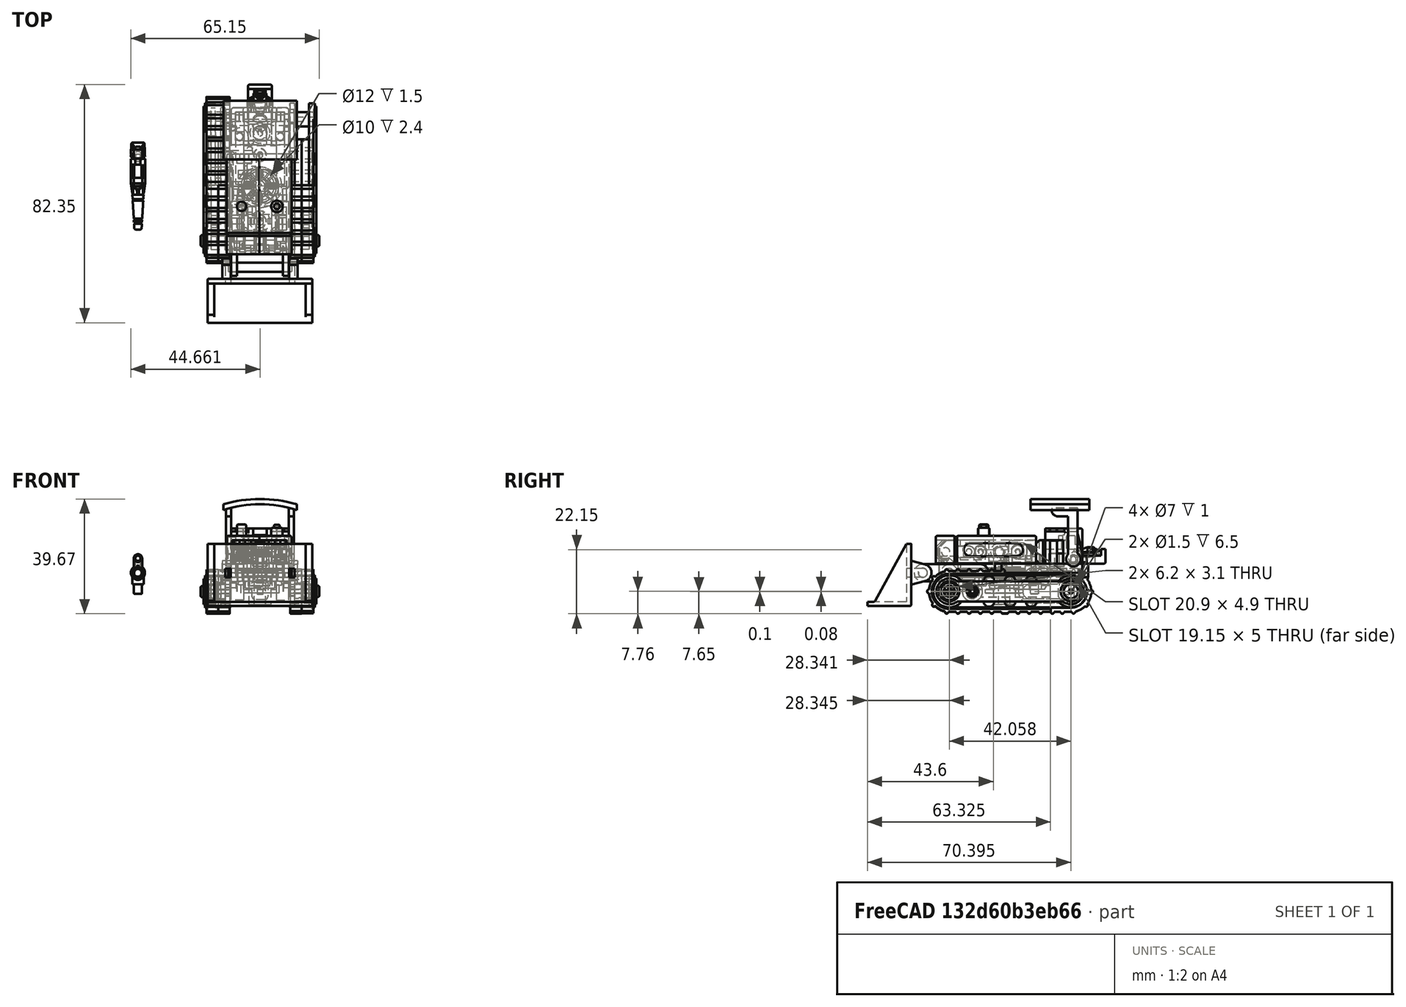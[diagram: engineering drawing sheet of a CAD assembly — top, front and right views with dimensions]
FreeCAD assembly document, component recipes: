
FREECAD ASSEMBLY — COMPONENT RECIPES ("Bonecrusher")

This assembly document has 22 components, labeled P0..P21 below (a component is one placed body or linked part). 22 of them carry a construction recipe — the FreeCAD feature program that regenerates the part from scratch, quoted from this document or its linked companion documents; the rest are supplied as boundary geometry only. No exploded tour is included for this assembly.
NOTE — this tour is split across 4 documents so each fits a 32k-token context. This is document 1: the component sections continue in the remaining 3 documents, each repeating the header above.
COMPONENT P0 — recipe-attached ("Right_Arm_Shield", modeled in this document).
Construction recipe (the document's own serialized feature program — sketch geometry with constraints, then the solid features built on it; lengths are millimeters unless a unit is written):

FEATURE [Sketcher::SketchObject] Sketch012
  ArcFitTolerance = 1e-06
  AttachmentSupport = -> [XY_Plane003]
  FullyConstrained = true
  MakeInternals = false
  MapMode = 5
  sketch-geometry (4):
    g0: LineSegment StartX=-34.7 StartY=4.75 StartZ=0 EndX=-34.7 EndY=-4.75 EndZ=0
    g1: LineSegment StartX=-34.7 StartY=-4.75 StartZ=0 EndX=0 EndY=-4.75 EndZ=0
    g2: LineSegment StartX=0 StartY=-4.75 StartZ=0 EndX=0 EndY=4.75 EndZ=0
    g3: LineSegment StartX=0 StartY=4.75 StartZ=0 EndX=-34.7 EndY=4.75 EndZ=0
  constraints (12):
    c: Coincident(g0,g1)
    c: Coincident(g1,g2)
    c: Coincident(g2,g3)
    c: Coincident(g3,g0)
    c: Vertical(g0)
    c: Vertical(g2)
    c: Horizontal(g1)
    c: Horizontal(g3)
    c: PointOnObject(g1,g-2)
    c: DistanceX(g3,g3) = 34.7
    c: DistanceY(g0,g0) = 9.5
    c: DistanceY(g-1,g2) = 4.75
FEATURE [PartDesign::Pad] Pad002
  Direction = (0,0,1)
  Length = 10.2
  Length2 = 10
  Profile = -> Sketch012
  ReferenceAxis = -> Sketch012 [N_Axis]
  Refine = true
  Suppressed = false
  Type = 0
FEATURE [Sketcher::SketchObject] Sketch013
  ArcFitTolerance = 1e-06
  AttachmentSupport = -> [Pad002]
  ExternalGeometry = -> [Pad002]
  FullyConstrained = true
  MakeInternals = false
  MapMode = 5
  Placement = pos=(0,0,10.2) rot=(0,0,1;0rad)
  sketch-geometry (4):
    g0: LineSegment StartX=-34.7 StartY=4.75 StartZ=0 EndX=-34.7 EndY=-3.25 EndZ=0
    g1: LineSegment StartX=-34.7 StartY=-3.25 StartZ=0 EndX=0 EndY=-3.25 EndZ=0
    g2: LineSegment StartX=0 StartY=-3.25 StartZ=0 EndX=0 EndY=4.75 EndZ=0
    g3: LineSegment StartX=0 StartY=4.75 StartZ=0 EndX=-34.7 EndY=4.75 EndZ=0
  constraints (11):
    c: Coincident(g0,g1)
    c: Coincident(g1,g2)
    c: Coincident(g2,g3)
    c: Coincident(g3,g0)
    c: Vertical(g0)
    c: Vertical(g2)
    c: Horizontal(g1)
    c: Horizontal(g3)
    c: Coincident(g0,g-3)
    c: PointOnObject(g1,g-4)
    c: DistanceY(g2,g2) = 8
FEATURE [PartDesign::Pocket] Pocket010
  BaseFeature = -> Pad002
  Direction = (0,0,-1)
  Length = 8.4
  Length2 = 5
  Profile = -> Sketch013
  ReferenceAxis = -> Sketch013 [N_Axis]
  Refine = true
  Suppressed = false
  Type = 0
FEATURE [Sketcher::SketchObject] Sketch014
  ArcFitTolerance = 1e-06
  AttachmentSupport = -> [Pocket010]
  ExternalGeometry = -> [Pocket010]
  FullyConstrained = true
  MakeInternals = false
  MapMode = 5
  Placement = pos=(0,0,1.8) rot=(0,0,1;0rad)
  sketch-geometry (4):
    g0: LineSegment StartX=-18.4 StartY=4.75 StartZ=0 EndX=-18.4 EndY=-3.25 EndZ=0
    g1: LineSegment StartX=-18.4 StartY=-3.25 StartZ=0 EndX=-7.1 EndY=-3.25 EndZ=0
    g2: LineSegment StartX=-7.1 StartY=-3.25 StartZ=0 EndX=-7.1 EndY=4.75 EndZ=0
    g3: LineSegment StartX=-7.1 StartY=4.75 StartZ=0 EndX=-18.4 EndY=4.75 EndZ=0
  constraints (12):
    c: Coincident(g0,g1)
    c: Coincident(g1,g2)
    c: Coincident(g2,g3)
    c: Coincident(g3,g0)
    c: Vertical(g0)
    c: Vertical(g2)
    c: Horizontal(g1)
    c: Horizontal(g3)
    c: DistanceX(g1,g-1) = 7.1
    c: DistanceX(g3,g3) = 11.3
    c: PointOnObject(g2,g-3)
    c: PointOnObject(g1,g-4)
FEATURE [PartDesign::Pad] Pad003
  BaseFeature = -> Pocket010
  Direction = (0,0,1)
  Length = 3.8
  Length2 = 10
  Profile = -> Sketch014
  ReferenceAxis = -> Sketch014 [N_Axis]
  Refine = true
  Suppressed = false
  Type = 0
FEATURE [Sketcher::SketchObject] Sketch015
  ArcFitTolerance = 1e-06
  AttachmentSupport = -> [Pad003]
  ExternalGeometry = -> [Pad003]
  FullyConstrained = true
  MakeInternals = false
  MapMode = 5
  Placement = pos=(0,0,1.8) rot=(0,0,1;0rad)
  sketch-geometry (1):
    g0: Circle CenterX=-22 CenterY=0.75 CenterZ=0 NormalX=0 NormalY=0 NormalZ=1 AngleXU=0 Radius=1.5
  constraints (3):
    c: Diameter(g0) = 3
    c: DistanceX(g-3,g0) = 12.7
    c: DistanceY(g0,g-3) = 4
FEATURE [PartDesign::Pad] Pad004
  BaseFeature = -> Pad003
  Direction = (0,0,1)
  Length = 7.5
  Length2 = 10
  Profile = -> Sketch015
  ReferenceAxis = -> Sketch015 [N_Axis]
  Refine = true
  Suppressed = false
  Type = 0
FEATURE [PartDesign::Fillet] Fillet002
  Base = -> Pad004 [Edge7,Edge2,Edge1,Edge10,Edge8]
  BaseFeature = -> Pad004
  Radius = 0.5
  Refine = true
  SupportTransform = false
  Suppressed = false
  UseAllEdges = false
FEATURE [Sketcher::SketchObject] Sketch016
  ArcFitTolerance = 1e-06
  AttachmentSupport = -> [Fillet002]
  ExternalGeometry = -> [Fillet002]
  FullyConstrained = true
  MakeInternals = false
  MapMode = 5
  Placement = pos=(0,0,5.6) rot=(0,0,1;0rad)
  sketch-geometry (4):
    g0: LineSegment StartX=-17.15 StartY=3.5 StartZ=0 EndX=-17.15 EndY=-3.25 EndZ=0
    g1: LineSegment StartX=-17.15 StartY=-3.25 StartZ=0 EndX=-8.35 EndY=-3.25 EndZ=0
    g2: LineSegment StartX=-8.35 StartY=-3.25 StartZ=0 EndX=-8.35 EndY=3.5 EndZ=0
    g3: LineSegment StartX=-8.35 StartY=3.5 StartZ=0 EndX=-17.15 EndY=3.5 EndZ=0
  constraints (12):
    c: Coincident(g0,g1)
    c: Coincident(g1,g2)
    c: Coincident(g2,g3)
    c: Coincident(g3,g0)
    c: Vertical(g0)
    c: Vertical(g2)
    c: Horizontal(g1)
    c: Horizontal(g3)
    c: DistanceY(g0,g-3) = 1.25
    c: PointOnObject(g0,g-4)
    c: DistanceX(g2,g-3) = 1.25
    c: DistanceX(g-3,g0) = 1.25
FEATURE [PartDesign::Pocket] Pocket011
  BaseFeature = -> Fillet002
  Direction = (0,0,-1)
  Length = 3.81
  Length2 = 5
  Profile = -> Sketch016
  ReferenceAxis = -> Sketch016 [N_Axis]
  Refine = true
  Suppressed = false
  Type = 0
FEATURE [Sketcher::SketchObject] Sketch017
  ArcFitTolerance = 1e-06
  AttachmentSupport = -> [Pocket011]
  ExternalGeometry = -> [Pocket011]
  FullyConstrained = false
  MakeInternals = false
  MapMode = 5
  Placement = pos=(0,0,1.79) rot=(0,0,1;0rad)
  sketch-geometry (4):
    g0: LineSegment StartX=-8.35 StartY=2.75 StartZ=0 EndX=-11.5 EndY=2.75 EndZ=0
    g1: ArcOfCircle CenterX=-11.5 CenterY=0.75 CenterZ=0 NormalX=0 NormalY=0 NormalZ=1 AngleXU=0 Radius=2 StartAngle=1.5708 EndAngle=4.71238
    g2: LineSegment StartX=-11.5 StartY=-1.25 StartZ=0 EndX=-8.35 EndY=-1.25 EndZ=0
    g3: LineSegment StartX=-8.35 StartY=-1.25 StartZ=0 EndX=-8.35 EndY=2.75 EndZ=0
  constraints (12):
    c: Horizontal(g0)
    c: Coincident(g1,g0)
    c: Coincident(g2,g1)
    c: Horizontal(g2)
    c: Coincident(g3,g2)
    c: Coincident(g3,g0)
    c: Vertical(g3)
    c: PointOnObject(g0,g-3)
    c: DistanceY(g2,g0) = 4
    c: DistanceY(g0,g-4) = 2
    c: Diameter(g1) = 4
    c: DistanceX(g0,g0) = 3.15
FEATURE [Sketcher::SketchObject] Sketch018
  ArcFitTolerance = 1e-06
  AttachmentSupport = -> [Pocket011]
  ExternalGeometry = -> [Pocket011]
  FullyConstrained = true
  MakeInternals = false
  MapMode = 5
  Placement = pos=(0,0,5.6) rot=(0,0,1;0rad)
  sketch-geometry (4):
    g0: LineSegment StartX=-8.35 StartY=2.75 StartZ=0 EndX=-8.35 EndY=-1.25 EndZ=0
    g1: LineSegment StartX=-8.35 StartY=-1.25 StartZ=0 EndX=-7.1 EndY=-1.25 EndZ=0
    g2: LineSegment StartX=-7.1 StartY=-1.25 StartZ=0 EndX=-7.1 EndY=2.75 EndZ=0
    g3: LineSegment StartX=-7.1 StartY=2.75 StartZ=0 EndX=-8.35 EndY=2.75 EndZ=0
  constraints (12):
    c: Coincident(g0,g1)
    c: Coincident(g1,g2)
    c: Coincident(g2,g3)
    c: Coincident(g3,g0)
    c: Vertical(g0)
    c: Vertical(g2)
    c: Horizontal(g1)
    c: Horizontal(g3)
    c: DistanceY(g2,g-3) = 2
    c: PointOnObject(g0,g-4)
    c: PointOnObject(g2,g-5)
    c: DistanceY(g1,g2) = 4
FEATURE [PartDesign::Pocket] Pocket012
  BaseFeature = -> Pocket011
  Direction = (0,0,-1)
  Length = 1.25
  Length2 = 5
  Profile = -> Sketch018
  ReferenceAxis = -> Sketch018 [N_Axis]
  Refine = true
  Suppressed = false
  Type = 0
FEATURE [PartDesign::Pad] Pad005
  BaseFeature = -> Pocket012
  Direction = (0,0,1)
  Length = 2.56
  Length2 = 10
  Profile = -> Sketch017
  ReferenceAxis = -> Sketch017 [N_Axis]
  Refine = true
  Suppressed = false
  Type = 0
FEATURE [Sketcher::SketchObject] Sketch019
  ArcFitTolerance = 1e-06
  AttachmentSupport = -> [Pad005]
  ExternalGeometry = -> [Pad005]
  FullyConstrained = true
  MakeInternals = false
  MapMode = 5
  Placement = pos=(0,0,1.79) rot=(0,0,1;0rad)
  sketch-geometry (1):
    g0: Circle CenterX=-15.5 CenterY=0.75 CenterZ=0 NormalX=0 NormalY=0 NormalZ=1 AngleXU=0 Radius=1.9
  constraints (3):
    c: DistanceY(g0,g-3) = 4
    c: Diameter(g0) = 3.8
    c: DistanceX(g-5,g0) = 1.65
FEATURE [PartDesign::Pad] Pad006
  BaseFeature = -> Pad005
  Direction = (0,0,1)
  Length = 5
  Length2 = 10
  Profile = -> Sketch019
  ReferenceAxis = -> Sketch019 [N_Axis]
  Refine = true
  Suppressed = false
  Type = 0
FEATURE [Sketcher::SketchObject] Sketch020
  ArcFitTolerance = 1e-06
  AttachmentSupport = -> [Pad006]
  ExternalGeometry = -> [Pad006]
  FullyConstrained = true
  MakeInternals = false
  MapMode = 5
  Placement = pos=(0,0,4.35) rot=(0,0,1;0rad)
  sketch-geometry (1):
    g0: Circle CenterX=-11.5 CenterY=0.75 CenterZ=0 NormalX=0 NormalY=0 NormalZ=1 AngleXU=0 Radius=1.05
  constraints (3):
    c: DistanceY(g0,g-4) = 2
    c: DistanceX(g0,g-3) = 4.4
    c: Diameter(g0) = 2.1
FEATURE [PartDesign::Pocket] Pocket014
  BaseFeature = -> Pad006
  Direction = (0,0,-1)
  Length = 2.56
  Length2 = 5
  Profile = -> Sketch020
  ReferenceAxis = -> Sketch020 [N_Axis]
  Refine = true
  Suppressed = false
  Type = 0
FEATURE [Sketcher::SketchObject] Sketch021
  ArcFitTolerance = 1e-06
  AttachmentSupport = -> [Pocket014]
  ExternalGeometry = -> [Pocket014]
  FullyConstrained = true
  MakeInternals = false
  MapMode = 5
  Placement = pos=(0,0,6.79) rot=(0,0,1;0rad)
  sketch-geometry (1):
    g0: Circle CenterX=-15.5 CenterY=0.75 CenterZ=0 NormalX=0 NormalY=0 NormalZ=1 AngleXU=0 Radius=0.75
  constraints (2):
    c: Diameter(g0) = 1.5
    c: Coincident(g0,g-3)
FEATURE [PartDesign::Pocket] Pocket015
  BaseFeature = -> Pocket014
  Direction = (0,0,-1)
  Length = 5
  Length2 = 5
  Profile = -> Sketch021
  ReferenceAxis = -> Sketch021 [N_Axis]
  Refine = true
  Suppressed = false
  Type = 0
FEATURE [Sketcher::SketchObject] Sketch022
  ArcFitTolerance = 1e-06
  AttachmentSupport = -> [Pocket015]
  ExternalGeometry = -> [Pocket015]
  FullyConstrained = true
  MakeInternals = false
  MapMode = 5
  Placement = pos=(0,0,0) rot=(1,0,0;3.14159rad)
  sketch-geometry (8):
    g0: ArcOfCircle CenterX=-27.95 CenterY=0 CenterZ=0 NormalX=0 NormalY=0 NormalZ=1 AngleXU=0 Radius=2.25 StartAngle=1.5708 EndAngle=4.71239
    g1: ArcOfCircle CenterX=-11.95 CenterY=1e-16 CenterZ=0 NormalX=0 NormalY=0 NormalZ=1 AngleXU=0 Radius=2.25 StartAngle=4.71239 EndAngle=7.85398
    g2: LineSegment StartX=-27.95 StartY=2.25 StartZ=0 EndX=-11.95 EndY=2.25 EndZ=0
    g3: LineSegment StartX=-27.95 StartY=-2.25 StartZ=0 EndX=-11.95 EndY=-2.25 EndZ=0
    g4: LineSegment StartX=-7.45 StartY=4.75 StartZ=0 EndX=-7.45 EndY=-4.75 EndZ=0
    g5: LineSegment StartX=-7.45 StartY=-4.75 StartZ=0 EndX=-6.45 EndY=-4.75 EndZ=0
    g6: LineSegment StartX=-6.45 StartY=-4.75 StartZ=0 EndX=-6.45 EndY=4.75 EndZ=0
    g7: LineSegment StartX=-6.45 StartY=4.75 StartZ=0 EndX=-7.45 EndY=4.75 EndZ=0
  constraints (22):
    c: Tangent(g0,g2) = 1.5708
    c: Tangent(g0,g3) = -1.5708
    c: Tangent(g1,g2) = 1.5708
    c: Tangent(g1,g3) = -1.5708
    c: Equal(g0,g1)
    c: Horizontal(g3)
    c: PointOnObject(g0,g-1)
    c: Diameter(g0) = 4.5
    c: DistanceX(g-3,g0) = 6.75
    c: DistanceX(g0,g1) = 16
    c: Coincident(g4,g5)
    c: Coincident(g5,g6)
    c: Coincident(g6,g7)
    c: Coincident(g7,g4)
    c: Vertical(g4)
    c: Vertical(g6)
    c: Horizontal(g5)
    c: Horizontal(g7)
    c: PointOnObject(g6,g-4)
    c: PointOnObject(g5,g-5)
    c: DistanceX(g1,g4) = 4.5
    c: DistanceX(g4,g6) = 1
FEATURE [PartDesign::Pocket] Pocket016
  BaseFeature = -> Pocket015
  Direction = (0,0,1)
  Length = 0.3
  Length2 = 5
  Profile = -> Sketch022
  ReferenceAxis = -> Sketch022 [N_Axis]
  Refine = true
  Suppressed = false
  Type = 0
FEATURE [Sketcher::SketchObject] Sketch023
  ArcFitTolerance = 1e-06
  AttachmentSupport = -> [Pocket016]
  ExternalGeometry = -> [Pocket016]
  FullyConstrained = true
  MakeInternals = false
  MapMode = 5
  Placement = pos=(0,-4.75,0) rot=(1,0,0;1.5708rad)
  sketch-geometry (4):
    g0: LineSegment StartX=-7.45 StartY=10.2 StartZ=0 EndX=-7.45 EndY=0 EndZ=0
    g1: LineSegment StartX=-7.45 StartY=0 StartZ=0 EndX=-6.45 EndY=0 EndZ=0
    g2: LineSegment StartX=-6.45 StartY=0 StartZ=0 EndX=-6.45 EndY=10.2 EndZ=0
    g3: LineSegment StartX=-6.45 StartY=10.2 StartZ=0 EndX=-7.45 EndY=10.2 EndZ=0
  constraints (11):
    c: Coincident(g0,g1)
    c: Coincident(g1,g2)
    c: Coincident(g2,g3)
    c: Coincident(g3,g0)
    c: Vertical(g0)
    c: Vertical(g2)
    c: Horizontal(g1)
    c: Horizontal(g3)
    c: DistanceX(g3,g3) = 1
    c: Coincident(g0,g-3)
    c: PointOnObject(g0,g-4)
FEATURE [PartDesign::Pocket] Pocket017
  BaseFeature = -> Pocket016
  Direction = (0,1,-2e-16)
  Length = 0.3
  Length2 = 5
  Profile = -> Sketch023
  ReferenceAxis = -> Sketch023 [N_Axis]
  Refine = true
  Suppressed = false
  Type = 0
FEATURE [PartDesign::Fillet] Fillet003
  Base = -> Pocket017 [Edge90,Edge91,Edge89,Edge92]
  BaseFeature = -> Pocket017
  Radius = 0.2
  Refine = true
  SupportTransform = false
  Suppressed = false
  UseAllEdges = false
FEATURE [PartDesign::Fillet] Fillet004
  Base = -> Fillet003 [Edge5,Edge94,Edge20,Edge19,Edge18,Edge17,Edge93,Edge97,Edge96,Edge95]
  BaseFeature = -> Fillet003
  Radius = 0.2
  Refine = true
  SupportTransform = false
  Suppressed = false
  UseAllEdges = false
FEATURE [Sketcher::SketchObject] Sketch036
  ArcFitTolerance = 1e-06
  AttachmentSupport = -> [Fillet004]
  ExternalGeometry = -> [Fillet004]
  FullyConstrained = true
  MakeInternals = false
  MapMode = 5
  Placement = pos=(0,-4.75,0) rot=(1,0,0;1.5708rad)
  sketch-geometry (1):
    g0: Circle CenterX=-16.6 CenterY=5.1 CenterZ=0 NormalX=0 NormalY=0 NormalZ=1 AngleXU=0 Radius=1.625
  constraints (3):
    c: Diameter(g0) = 3.25
    c: DistanceY(g0,g-3) = 5.1
    c: DistanceX(g0,g-4) = 16.6
FEATURE [PartDesign::Pad] Pad012
  BaseFeature = -> Fillet004
  Direction = (0,-1,2e-16)
  Length = 4
  Length2 = 10
  Profile = -> Sketch036
  ReferenceAxis = -> Sketch036 [N_Axis]
  Refine = true
  Suppressed = false
  Type = 0
FEATURE [PartDesign::Fillet] Fillet008
  Base = -> Pad012 [Edge116]
  BaseFeature = -> Pad012
  Radius = 0.5
  Refine = true
  SupportTransform = false
  Suppressed = false
  UseAllEdges = false
FEATURE [PartDesign::Fillet] Fillet020
  Base = -> Fillet008 [Edge89,Edge85]
  BaseFeature = -> Fillet008
  Radius = 0.5
  Refine = true
  SupportTransform = false
  Suppressed = false
  UseAllEdges = false
FEATURE [Sketcher::SketchObject] Sketch282
  ArcFitTolerance = 1e-06
  AttachmentSupport = -> [Fillet020]
  ExternalGeometry = -> [Fillet020]
  FullyConstrained = true
  MakeInternals = false
  MapMode = 5
  Placement = pos=(0,0,10.2) rot=(0,0,1;0rad)
  sketch-geometry (12):
    g0: LineSegment StartX=0 StartY=-3.25 StartZ=0 EndX=0 EndY=-4.25 EndZ=0
    g1: ArcOfCircle CenterX=-0.5 CenterY=-4.25 CenterZ=0 NormalX=0 NormalY=0 NormalZ=1 AngleXU=0 Radius=0.5 StartAngle=4.71239 EndAngle=6.28319
    g2: LineSegment StartX=-0.5 StartY=-4.75 StartZ=0 EndX=-6.25 EndY=-4.75 EndZ=0
    g3: ArcOfCircle CenterX=-6.25 CenterY=-4.55 CenterZ=0 NormalX=0 NormalY=0 NormalZ=1 AngleXU=0 Radius=0.2 StartAngle=3.14159 EndAngle=4.71239
    g4: LineSegment StartX=-6.45 StartY=-4.55 StartZ=0 EndX=-6.45 EndY=-4.45 EndZ=0
    g5: LineSegment StartX=-6.45 StartY=-4.45 StartZ=0 EndX=-7.45 EndY=-4.45 EndZ=0
    g6: LineSegment StartX=-7.45 StartY=-4.45 StartZ=0 EndX=-7.45 EndY=-4.55 EndZ=0
    g7: ArcOfCircle CenterX=-7.65 CenterY=-4.55 CenterZ=0 NormalX=0 NormalY=0 NormalZ=1 AngleXU=0 Radius=0.2 StartAngle=4.71239 EndAngle=6.28319
    g8: LineSegment StartX=-7.65 StartY=-4.75 StartZ=0 EndX=-34.2 EndY=-4.75 EndZ=0
    g9: ArcOfCircle CenterX=-34.2 CenterY=-4.25 CenterZ=0 NormalX=0 NormalY=0 NormalZ=1 AngleXU=0 Radius=0.5 StartAngle=3.14159 EndAngle=4.71239
    g10: LineSegment StartX=-34.7 StartY=-4.25 StartZ=0 EndX=-34.7 EndY=-3.25 EndZ=0
    g11: LineSegment StartX=-34.7 StartY=-3.25 StartZ=0 EndX=0 EndY=-3.25 EndZ=0
  constraints (24):
    c: Coincident(g0,g-14)
    c: Coincident(g0,g-14)
    c: Coincident(g1,g0)
    c: Tangent(g1,g-13) = -1.5708
    c: Coincident(g2,g1)
    c: Coincident(g2,g-12)
    c: Coincident(g3,g2)
    c: Tangent(g3,g-11) = -1.5708
    c: Coincident(g5,g4)
    c: Coincident(g5,g-9)
    c: Coincident(g6,g5)
    c: Coincident(g6,g-8)
    c: Coincident(g7,g6)
    c: Tangent(g7,g-7) = -1.5708
    c: Coincident(g9,g8)
    c: Tangent(g9,g-5) = -1.5708
    c: Coincident(g11,g10)
    c: Coincident(g11,g0)
    c: Coincident(g4,g3)
    c: Coincident(g8,g7)
    c: Coincident(g-6,g8)
    c: Coincident(g10,g-4)
    c: Coincident(g10,g9)
    c: Coincident(g4,g-10)
FEATURE [PartDesign::Pad] Pad161
  BaseFeature = -> Fillet020
  Direction = (0,0,1)
  Length = 1
  Length2 = 10
  Profile = -> Sketch282
  ReferenceAxis = -> Sketch282 [N_Axis]
  Refine = true
  Suppressed = false
  Type = 0
FEATURE [PartDesign::Body] Body002  label="Right_Arm_Shield"
  AllowCompound = false
  Group = -> [Sketch012,Pad002,Sketch013,Pocket010,Sketch014,Pad003,Sketch015,Pad004,Fillet002,Sketch016,Pocket011,Sketch017,Sketch018,Pocket012,Pad005,Sketch019,Pad006,Sketch020,Pocket014,Sketch021,Pocket015,Sketch022,Pocket016,Sketch023,Pocket017,Fillet003,Fillet004,Sketch036,Pad012,Fillet008,Fillet020,Sketch282,Pad161]
  Origin = -> Origin003
  Placement = pos=(26.75,-55.7,8) rot=(0.58,-0.58,0.58;4.18879rad)
  Tip = -> Pad161
COMPONENT P1 — recipe-attached ("Front_Torso", modeled in this document).
Construction recipe (the document's own serialized feature program — sketch geometry with constraints, then the solid features built on it; lengths are millimeters unless a unit is written):

FEATURE [Sketcher::SketchObject] Sketch080
  ArcFitTolerance = 1e-06
  AttachmentSupport = -> [XY_Plane010]
  FullyConstrained = true
  MakeInternals = false
  MapMode = 5
  sketch-geometry (20):
    g0: LineSegment StartX=10 StartY=7.75 StartZ=0 EndX=10 EndY=-18.25 EndZ=0
    g1: LineSegment StartX=7.75 StartY=-19.25 StartZ=0 EndX=7.75 EndY=-33.25 EndZ=0
    g2: LineSegment StartX=5.65 StartY=-34.25 StartZ=0 EndX=5.65 EndY=-39.75 EndZ=0
    g3: LineSegment StartX=-5.65 StartY=-39.75 StartZ=0 EndX=-5.65 EndY=-34.25 EndZ=0
    g4: LineSegment StartX=-7.75 StartY=-33.25 StartZ=0 EndX=-7.75 EndY=-19.25 EndZ=0
    g5: LineSegment StartX=-10 StartY=-18.25 StartZ=0 EndX=-10 EndY=7.75 EndZ=0
    g6: ArcOfCircle CenterX=-9 CenterY=-18.25 CenterZ=0 NormalX=0 NormalY=0 NormalZ=1 AngleXU=0 Radius=1 StartAngle=3.14159 EndAngle=4.71239
    g7: LineSegment StartX=-9 StartY=-19.25 StartZ=0 EndX=-7.75 EndY=-19.25 EndZ=0
    g8: ArcOfCircle CenterX=-6.75 CenterY=-33.25 CenterZ=0 NormalX=0 NormalY=0 NormalZ=1 AngleXU=0 Radius=1 StartAngle=3.14159 EndAngle=4.71239
    g9: LineSegment StartX=-6.75 StartY=-34.25 StartZ=0 EndX=-5.65 EndY=-34.25 EndZ=0
    g10: ArcOfCircle CenterX=6.75 CenterY=-33.25 CenterZ=0 NormalX=0 NormalY=0 NormalZ=1 AngleXU=0 Radius=1 StartAngle=4.71239 EndAngle=6.28319
    g11: LineSegment StartX=5.65 StartY=-34.25 StartZ=0 EndX=6.75 EndY=-34.25 EndZ=0
    g12: ArcOfCircle CenterX=-4.65 CenterY=-39.75 CenterZ=0 NormalX=0 NormalY=0 NormalZ=1 AngleXU=0 Radius=1 StartAngle=3.14159 EndAngle=4.71239
    g13: ArcOfCircle CenterX=4.65 CenterY=-39.75 CenterZ=0 NormalX=0 NormalY=0 NormalZ=1 AngleXU=0 Radius=1 StartAngle=4.71239 EndAngle=6.28319
    g14: LineSegment StartX=4.65 StartY=-40.75 StartZ=0 EndX=-4.65 EndY=-40.75 EndZ=0
    g15: ArcOfCircle CenterX=9 CenterY=-18.25 CenterZ=0 NormalX=0 NormalY=0 NormalZ=1 AngleXU=0 Radius=1 StartAngle=4.71239 EndAngle=6.28319
    g16: LineSegment StartX=9 StartY=-19.25 StartZ=0 EndX=7.75 EndY=-19.25 EndZ=0
    g17: ArcOfCircle CenterX=-9 CenterY=7.75 CenterZ=0 NormalX=0 NormalY=0 NormalZ=1 AngleXU=0 Radius=1 StartAngle=1.5708 EndAngle=3.14159
    g18: ArcOfCircle CenterX=9 CenterY=7.75 CenterZ=0 NormalX=0 NormalY=0 NormalZ=1 AngleXU=0 Radius=1 StartAngle=0 EndAngle=1.5708
    g19: LineSegment StartX=-9 StartY=8.75 StartZ=0 EndX=9 EndY=8.75 EndZ=0
  constraints (68):
    c: Vertical(g0)
    c: Vertical(g1)
    c: Vertical(g2)
    c: Vertical(g3)
    c: Vertical(g4)
    c: Vertical(g5)
    c: DistanceY(g0,g0) = 26
    c: DistanceY(g5,g5) = 26
    c: DistanceX(g1,g0) = 2.25
    c: DistanceX(g5,g4) = 2.25
    c: DistanceY(g1,g1) = 14
    c: DistanceY(g4,g4) = 14
    c: DistanceX(g4,g3) = 2.1
    c: DistanceX(g2,g1) = 2.1
    c: DistanceY(g3,g3) = 5.5
    c: DistanceY(g-1,g5) = 7.75
    c: DistanceX(g5,g0) = 20
    c: DistanceX(g5,g-1) = 10
    c: Coincident(g6,g5)
    c: Coincident(g7,g6)
    c: Coincident(g7,g4)
    c: Horizontal(g7)
    c: Diameter(g6) = 2
    c: DistanceX(g6,g6) = 0
    c: DistanceY(g6,g5) = 0
    c: Coincident(g8,g4)
    c: Coincident(g9,g8)
    c: Coincident(g9,g3)
    c: Horizontal(g9)
    c: Diameter(g8) = 2
    c: DistanceX(g8,g8) = 0
    c: DistanceY(g8,g4) = 0
    c: Coincident(g10,g1)
    c: Coincident(g11,g2)
    c: Coincident(g11,g10)
    c: Horizontal(g11)
    c: Diameter(g10) = 2
    c: DistanceX(g10,g10) = 0
    c: DistanceY(g10,g1) = 0
    c: Coincident(g12,g3)
    c: Coincident(g13,g2)
    c: Coincident(g14,g13)
    c: Coincident(g14,g12)
    c: Horizontal(g14)
    c: Diameter(g12) = 2
    c: Diameter(g13) = 2
    c: DistanceY(g12,g3) = 0
    c: DistanceY(g13,g2) = 0
    c: DistanceX(g13,g13) = 0
    c: DistanceX(g12,g12) = 0
    c: Coincident(g15,g0)
    c: Coincident(g16,g15)
    c: Coincident(g16,g1)
    c: Horizontal(g16)
    c: Diameter(g15) = 2
    c: DistanceY(g15,g0) = 0
    c: DistanceX(g15,g15) = 0
    c: DistanceY(g2,g2) = 5.5
    c: Coincident(g17,g5)
    c: Coincident(g18,g0)
    c: Coincident(g19,g17)
    c: Coincident(g19,g18)
    c: Horizontal(g19)
    c: Diameter(g18) = 2
    c: Diameter(g17) = 2
    c: DistanceX(g17,g17) = 0
    c: DistanceX(g18,g18) = 0
    c: DistanceY(g0,g18) = 0
FEATURE [PartDesign::Pad] Pad042
  Direction = (0,0,1)
  Length = 1.7
  Length2 = 10
  Profile = -> Sketch080
  ReferenceAxis = -> Sketch080 [N_Axis]
  Refine = true
  Suppressed = false
  Type = 0
FEATURE [PartDesign::Plane] DatumPlane012
  AttachmentSupport = -> [Pad042]
  Length = 61.4673
  MapMode = 5
  Placement = pos=(0,0,1.7) rot=(0,0,1;0rad)
  ResizeMode = 0
  Width = 77.2173
FEATURE [Sketcher::SketchObject] Sketch081
  ArcFitTolerance = 1e-06
  AttachmentSupport = -> [DatumPlane012]
  FullyConstrained = true
  MakeInternals = false
  MapMode = 5
  Placement = pos=(0,0,1.7) rot=(0,0,1;0rad)
  sketch-geometry (4):
    g0: LineSegment StartX=-4.5 StartY=8.75 StartZ=0 EndX=4.5 EndY=8.75 EndZ=0
    g1: LineSegment StartX=4.5 StartY=8.75 StartZ=0 EndX=4.5 EndY=10.75 EndZ=0
    g2: LineSegment StartX=4.5 StartY=10.75 StartZ=0 EndX=-4.5 EndY=10.75 EndZ=0
    g3: LineSegment StartX=-4.5 StartY=10.75 StartZ=0 EndX=-4.5 EndY=8.75 EndZ=0
  constraints (12):
    c: Coincident(g0,g1)
    c: Coincident(g1,g2)
    c: Coincident(g2,g3)
    c: Coincident(g3,g0)
    c: Horizontal(g0)
    c: Horizontal(g2)
    c: Vertical(g1)
    c: Vertical(g3)
    c: PointOnObject(g0,g-3)
    c: DistanceX(g2,g2) = 9
    c: DistanceY(g3,g3) = 2
    c: DistanceX(g0,g-3) = 5.5
FEATURE [PartDesign::Pad] Pad043
  BaseFeature = -> Pad042
  Direction = (0,0,1)
  Length = 4.8
  Length2 = 10
  Profile = -> Sketch081
  ReferenceAxis = -> Sketch081 [N_Axis]
  Refine = true
  Reversed = true
  Suppressed = false
  Type = 0
FEATURE [PartDesign::Plane] DatumPlane013
  AttachmentSupport = -> [Pad043]
  Length = 60
  MapMode = 5
  Placement = pos=(0,10.75,0) rot=(0,0.707107,0.707107;3.14159rad)
  ResizeMode = 0
  Width = 60
FEATURE [Sketcher::SketchObject] Sketch082
  ArcFitTolerance = 1e-06
  AttachmentSupport = -> [DatumPlane013]
  ExternalGeometry = -> [DatumPlane012,Pad043]
  FullyConstrained = true
  MakeInternals = false
  MapMode = 5
  Placement = pos=(0,10.75,0) rot=(0,0.707107,0.707107;3.14159rad)
  sketch-geometry (4):
    g0: LineSegment StartX=-3.1 StartY=1.7 StartZ=0 EndX=-3.1 EndY=-1.3 EndZ=0
    g1: LineSegment StartX=-3.1 StartY=-1.3 StartZ=0 EndX=3.1 EndY=-1.3 EndZ=0
    g2: LineSegment StartX=3.1 StartY=-1.3 StartZ=0 EndX=3.1 EndY=1.7 EndZ=0
    g3: LineSegment StartX=3.1 StartY=1.7 StartZ=0 EndX=-3.1 EndY=1.7 EndZ=0
  constraints (12):
    c: Coincident(g0,g1)
    c: Coincident(g1,g2)
    c: Coincident(g2,g3)
    c: Coincident(g3,g0)
    c: Vertical(g0)
    c: Vertical(g2)
    c: Horizontal(g1)
    c: Horizontal(g3)
    c: DistanceX(g-4,g0) = 1.4
    c: DistanceX(g2,g-5) = 1.4
    c: DistanceY(g-4,g0) = 1.8
    c: PointOnObject(g0,g-3)
FEATURE [PartDesign::Pocket] Pocket044
  BaseFeature = -> Pad043
  Direction = (0,-1,2e-16)
  Length = 2
  Length2 = 5
  Profile = -> Sketch082
  ReferenceAxis = -> Sketch082 [N_Axis]
  Refine = true
  Suppressed = false
  Type = 0
FEATURE [Sketcher::SketchObject] Sketch083
  ArcFitTolerance = 1e-06
  AttacherType = Attacher::AttachEngine3D
  AttachmentSupport = -> [DatumPlane012]
  FullyConstrained = true
  MakeInternals = false
  MapMode = 5
  Placement = pos=(0,0,1.7) rot=(0,0,1;0rad)
  sketch-geometry (4):
    g0: Circle CenterX=0 CenterY=0 CenterZ=0 NormalX=0 NormalY=0 NormalZ=1 AngleXU=0 Radius=0.75
    g1: Circle CenterX=-7.05 CenterY=-1.25 CenterZ=0 NormalX=0 NormalY=0 NormalZ=1 AngleXU=0 Radius=1.3
    g2: Circle CenterX=7.05 CenterY=-1.25 CenterZ=0 NormalX=0 NormalY=0 NormalZ=1 AngleXU=0 Radius=1.3
    g3: Circle CenterX=0 CenterY=-18.25 CenterZ=0 NormalX=0 NormalY=0 NormalZ=1 AngleXU=0 Radius=0.65
  constraints (11):
    c: Coincident(g0,g-1)
    c: Diameter(g0) = 1.5
    c: DistanceY(g1,g-3) = 10
    c: DistanceY(g2,g-4) = 10
    c: Diameter(g1) = 2.6
    c: Diameter(g2) = 2.6
    c: PointOnObject(g3,g-2)
    c: Diameter(g3) = 1.3
    c: DistanceY(g3,g-3) = 27
    c: DistanceX(g2,g-4) = 2.95
    c: DistanceX(g-3,g1) = 2.95
FEATURE [PartDesign::Pocket] Pocket045
  BaseFeature = -> Pocket044
  Direction = (0,0,-1)
  Length = 1.7
  Length2 = 5
  Profile = -> Sketch083
  ReferenceAxis = -> Sketch083 [N_Axis]
  Refine = true
  Suppressed = false
  Type = 0
FEATURE [Sketcher::SketchObject] Sketch084
  ArcFitTolerance = 1e-06
  AttachmentSupport = -> [DatumPlane012]
  FullyConstrained = true
  MakeInternals = false
  MapMode = 5
  Placement = pos=(0,0,1.7) rot=(0,0,1;0rad)
  sketch-geometry (1):
    g0: Circle CenterX=0 CenterY=0 CenterZ=0 NormalX=0 NormalY=0 NormalZ=1 AngleXU=0 Radius=2.5
  constraints (2):
    c: Coincident(g0,g-1)
    c: Diameter(g0) = 5
FEATURE [PartDesign::Pocket] Pocket046
  BaseFeature = -> Pocket045
  Direction = (0,0,-1)
  Length = 1
  Length2 = 5
  Profile = -> Sketch084
  ReferenceAxis = -> Sketch084 [N_Axis]
  Refine = true
  Suppressed = false
  Type = 0
FEATURE [Sketcher::SketchObject] Sketch085
  ArcFitTolerance = 1e-06
  AttachmentSupport = -> [DatumPlane012]
  ExternalGeometry = -> [Pocket046]
  FullyConstrained = true
  MakeInternals = false
  MapMode = 5
  Placement = pos=(0,0,1.7) rot=(0,0,1;0rad)
  sketch-geometry (4):
    g0: ArcOfCircle CenterX=-1.375 CenterY=4.95 CenterZ=0 NormalX=0 NormalY=0 NormalZ=1 AngleXU=0 Radius=1 StartAngle=1.5708 EndAngle=4.71239
    g1: ArcOfCircle CenterX=1.375 CenterY=4.95 CenterZ=0 NormalX=0 NormalY=0 NormalZ=1 AngleXU=0 Radius=1 StartAngle=4.71239 EndAngle=7.85398
    g2: LineSegment StartX=-1.375 StartY=5.95 StartZ=0 EndX=1.375 EndY=5.95 EndZ=0
    g3: LineSegment StartX=-1.375 StartY=3.95 StartZ=0 EndX=1.375 EndY=3.95 EndZ=0
  constraints (10):
    c: Tangent(g0,g2) = 1.5708
    c: Tangent(g0,g3) = -1.5708
    c: Tangent(g1,g2) = 1.5708
    c: Tangent(g1,g3) = -1.5708
    c: Equal(g0,g1)
    c: Horizontal(g3)
    c: DistanceY(g0,g-3) = 2.8
    c: Diameter(g0) = 2
    c: DistanceX(g0,g1) = 2.75
    c: DistanceX(g-1,g1) = 1.375
FEATURE [PartDesign::Pad] Pad044
  BaseFeature = -> Pocket046
  Direction = (0,0,1)
  Length = 0.5
  Length2 = 10
  Profile = -> Sketch085
  ReferenceAxis = -> Sketch085 [N_Axis]
  Refine = true
  Suppressed = false
  Type = 0
FEATURE [Sketcher::SketchObject] Sketch086
  ArcFitTolerance = 1e-06
  AttachmentSupport = -> [DatumPlane012]
  FullyConstrained = true
  MakeInternals = false
  MapMode = 5
  Placement = pos=(0,0,1.7) rot=(0,0,1;0rad)
  sketch-geometry (4):
    g0: LineSegment StartX=1.15 StartY=-40.75 StartZ=0 EndX=1.15 EndY=-27 EndZ=0
    g1: LineSegment StartX=1.15 StartY=-27 StartZ=0 EndX=-1.15 EndY=-27 EndZ=0
    g2: LineSegment StartX=-1.15 StartY=-27 StartZ=0 EndX=-1.15 EndY=-40.75 EndZ=0
    g3: LineSegment StartX=-1.15 StartY=-40.75 StartZ=0 EndX=1.15 EndY=-40.75 EndZ=0
  constraints (12):
    c: Coincident(g0,g1)
    c: Coincident(g1,g2)
    c: Coincident(g2,g3)
    c: Coincident(g3,g0)
    c: Vertical(g0)
    c: Vertical(g2)
    c: Horizontal(g1)
    c: Horizontal(g3)
    c: PointOnObject(g0,g-3)
    c: DistanceX(g1,g1) = 2.3
    c: DistanceY(g2,g2) = 13.75
    c: DistanceX(g-4,g2) = 4.5
FEATURE [PartDesign::Pad] Pad045
  BaseFeature = -> Pad044
  Direction = (0,0,1)
  Length = 2.5
  Length2 = 10
  Profile = -> Sketch086
  ReferenceAxis = -> Sketch086 [N_Axis]
  Refine = true
  Suppressed = false
  Type = 0
FEATURE [PartDesign::Plane] DatumPlane014
  AttachmentSupport = -> [Pad045]
  Length = 77.2173
  MapMode = 5
  Placement = pos=(1.15,0,0) rot=(0.57735,0.57735,0.57735;2.0944rad)
  ResizeMode = 0
  Width = 61.4673
FEATURE [Sketcher::SketchObject] Sketch087
  ArcFitTolerance = 1e-06
  AttachmentSupport = -> [DatumPlane014]
  ExternalGeometry = -> [Pad045]
  FullyConstrained = true
  MakeInternals = false
  MapMode = 5
  Placement = pos=(1.15,0,0) rot=(0.57735,0.57735,0.57735;2.0944rad)
  sketch-geometry (3):
    g0: LineSegment StartX=-27 StartY=1.7 StartZ=0 EndX=-27 EndY=4.2 EndZ=0
    g1: LineSegment StartX=-29.5 StartY=4.2 StartZ=0 EndX=-27 EndY=1.7 EndZ=0
    g2: LineSegment StartX=-27 StartY=4.2 StartZ=0 EndX=-29.5 EndY=4.2 EndZ=0
  constraints (7):
    c: Coincident(g0,g-4)
    c: Coincident(g0,g-4)
    c: PointOnObject(g1,g-3)
    c: Coincident(g1,g0)
    c: Angle(g-3,g1) = 2.35619
    c: Coincident(g2,g0)
    c: Coincident(g2,g1)
FEATURE [PartDesign::Pocket] Pocket047
  BaseFeature = -> Pad045
  Direction = (-1,0,0)
  Length = 2.3
  Length2 = 5
  Profile = -> Sketch087
  ReferenceAxis = -> Sketch087 [N_Axis]
  Refine = true
  Suppressed = false
  Type = 0
FEATURE [Sketcher::SketchObject] Sketch088
  ArcFitTolerance = 1e-06
  AttachmentSupport = -> [Pocket047]
  FullyConstrained = true
  MakeInternals = false
  MapMode = 5
  Placement = pos=(0,0,0) rot=(1,0,0;3.14159rad)
  sketch-geometry (6):
    g0: ArcOfCircle CenterX=-4.65 CenterY=39.75 CenterZ=0 NormalX=0 NormalY=0 NormalZ=1 AngleXU=0 Radius=1 StartAngle=1.5708 EndAngle=3.14159
    g1: ArcOfCircle CenterX=4.65 CenterY=39.75 CenterZ=0 NormalX=0 NormalY=0 NormalZ=1 AngleXU=0 Radius=1 StartAngle=-1.8e-15 EndAngle=1.5708
    g2: LineSegment StartX=-4.65 StartY=40.75 StartZ=0 EndX=4.65 EndY=40.75 EndZ=0
    g3: LineSegment StartX=5.65 StartY=34.25 StartZ=0 EndX=-5.65 EndY=34.25 EndZ=0
    g4: LineSegment StartX=5.65 StartY=39.75 StartZ=0 EndX=5.65 EndY=34.25 EndZ=0
    g5: LineSegment StartX=-5.65 StartY=39.75 StartZ=0 EndX=-5.65 EndY=34.25 EndZ=0
  constraints (16):
    c: Coincident(g0,g-3)
    c: Coincident(g0,g-4)
    c: Coincident(g2,g0)
    c: Coincident(g2,g1)
    c: Coincident(g4,g1)
    c: Vertical(g4)
    c: DistanceY(g4,g4) = 5.5
    c: Coincident(g5,g0)
    c: Vertical(g5)
    c: Coincident(g3,g5)
    c: Coincident(g3,g4)
    c: Coincident(g1,g-5)
    c: Coincident(g1,g-5)
    c: Horizontal(g3)
    c: Horizontal(g2)
    c: DistanceY(g0,g0) = 0
FEATURE [PartDesign::Pad] Pad046
  BaseFeature = -> Pocket047
  Direction = (0,0,-1)
  Length = 1.5
  Length2 = 10
  Profile = -> Sketch088
  ReferenceAxis = -> Sketch088 [N_Axis]
  Refine = true
  Suppressed = false
  Type = 0
FEATURE [Sketcher::SketchObject] Sketch089
  ArcFitTolerance = 1e-06
  AttachmentSupport = -> [Pad046]
  ExternalGeometry = -> [Pad046]
  FullyConstrained = true
  MakeInternals = false
  MapMode = 5
  Placement = pos=(0,0,0) rot=(1,0,0;3.14159rad)
  sketch-geometry (14):
    g0: LineSegment StartX=7.75 StartY=33.25 StartZ=0 EndX=7.75 EndY=19.25 EndZ=0
    g1: LineSegment StartX=7.75 StartY=19.25 StartZ=0 EndX=9 EndY=19.25 EndZ=0
    g2: ArcOfCircle CenterX=9 CenterY=18.25 CenterZ=0 NormalX=0 NormalY=0 NormalZ=1 AngleXU=0 Radius=1 StartAngle=0 EndAngle=1.5708
    g3: LineSegment StartX=10 StartY=18.25 StartZ=0 EndX=10 EndY=-7.75 EndZ=0
    g4: LineSegment StartX=9 StartY=-8.75 StartZ=0 EndX=-9 EndY=-8.75 EndZ=0
    g5: ArcOfCircle CenterX=-9 CenterY=-7.75 CenterZ=0 NormalX=0 NormalY=0 NormalZ=1 AngleXU=0 Radius=1 StartAngle=3.14159 EndAngle=4.71239
    g6: LineSegment StartX=-10 StartY=-7.75 StartZ=0 EndX=-10 EndY=18.25 EndZ=0
    g7: ArcOfCircle CenterX=-9 CenterY=18.25 CenterZ=0 NormalX=0 NormalY=0 NormalZ=1 AngleXU=0 Radius=1 StartAngle=1.5708 EndAngle=3.14159
    g8: LineSegment StartX=-9 StartY=19.25 StartZ=0 EndX=-7.75 EndY=19.25 EndZ=0
    g9: ArcOfCircle CenterX=-6.75 CenterY=33.25 CenterZ=0 NormalX=0 NormalY=0 NormalZ=1 AngleXU=0 Radius=1 StartAngle=1.5708 EndAngle=3.14159
    g10: ArcOfCircle CenterX=6.75 CenterY=33.25 CenterZ=0 NormalX=0 NormalY=0 NormalZ=1 AngleXU=0 Radius=1 StartAngle=9e-16 EndAngle=1.5708
    g11: LineSegment StartX=6.75 StartY=34.25 StartZ=0 EndX=-6.75 EndY=34.25 EndZ=0
    g12: LineSegment StartX=-7.75 StartY=33.25 StartZ=0 EndX=-7.75 EndY=19.25 EndZ=0
    g13: ArcOfCircle CenterX=9 CenterY=-7.75 CenterZ=0 NormalX=0 NormalY=0 NormalZ=1 AngleXU=0 Radius=1 StartAngle=4.71239 EndAngle=6.28319
  constraints (35):
    c: Coincident(g2,g-11)
    c: Coincident(g2,g1)
    c: Coincident(g2,g-11)
    c: Tangent(g3,g2) = 1.5708
    c: Coincident(g5,g-6)
    c: Coincident(g5,g4)
    c: Coincident(g5,g-6)
    c: Coincident(g6,g5)
    c: Coincident(g6,g-5)
    c: Coincident(g7,g-4)
    c: Coincident(g7,g6)
    c: Coincident(g8,g7)
    c: Coincident(g8,g-3)
    c: Horizontal(g8)
    c: Coincident(g0,g1)
    c: Radius(g9) = 1
    c: DistanceX(g9,g9) = 0
    c: DistanceY(g9,g9) = 0
    c: PointOnObject(g0,g-14)
    c: Coincident(g10,g0)
    c: Radius(g10) = 1
    c: DistanceY(g0,g10) = 0
    c: Tangent(g11,g10) = -1.5708
    c: Coincident(g11,g9)
    c: Coincident(g12,g9)
    c: Coincident(g12,g8)
    c: Vertical(g12)
    c: Coincident(g13,g3)
    c: Coincident(g13,g-9)
    c: Coincident(g4,g13)
    c: Horizontal(g4)
    c: Coincident(g4,g-9)
    c: Coincident(g0,g-14)
    c: Horizontal(g1)
    c: Coincident(g10,g-15)
FEATURE [PartDesign::Pad] Pad047
  BaseFeature = -> Pad046
  Direction = (0,0,-1)
  Length = 1.5
  Length2 = 10
  Profile = -> Sketch089
  ReferenceAxis = -> Sketch089 [N_Axis]
  Refine = true
  Suppressed = false
  Type = 0
FEATURE [Sketcher::SketchObject] Sketch090
  ArcFitTolerance = 1e-06
  AttachmentSupport = -> [Pad047]
  ExternalGeometry = -> [Pad047]
  FullyConstrained = true
  MakeInternals = false
  MapMode = 5
  Placement = pos=(0,0,-1.5) rot=(1,0,0;3.14159rad)
  sketch-geometry (22):
    g0: ArcOfCircle CenterX=-4.1 CenterY=-8.25 CenterZ=0 NormalX=0 NormalY=0 NormalZ=1 AngleXU=0 Radius=1 StartAngle=0 EndAngle=1.5708
    g1: LineSegment StartX=-3.1 StartY=-8.25 StartZ=0 EndX=-3.1 EndY=-8.75 EndZ=0
    g2: ArcOfCircle CenterX=-7.25 CenterY=18.75 CenterZ=0 NormalX=0 NormalY=0 NormalZ=1 AngleXU=0 Radius=1 StartAngle=4.71239 EndAngle=6.28319
    g3: LineSegment StartX=-6.25 StartY=18.75 StartZ=0 EndX=-6.25 EndY=32.75 EndZ=0
    g4: LineSegment StartX=-3.1 StartY=-8.75 StartZ=0 EndX=3.1 EndY=-8.75 EndZ=0
    g5: LineSegment StartX=3.1 StartY=-8.75 StartZ=0 EndX=3.1 EndY=-8.25 EndZ=0
    g6: ArcOfCircle CenterX=4.1 CenterY=-8.25 CenterZ=0 NormalX=0 NormalY=0 NormalZ=1 AngleXU=0 Radius=1 StartAngle=1.5708 EndAngle=3.14159
    g7: LineSegment StartX=4.1 StartY=-7.25 StartZ=0 EndX=8.5 EndY=-7.25 EndZ=0
    g8: LineSegment StartX=8.5 StartY=-7.25 StartZ=0 EndX=8.5 EndY=17.75 EndZ=0
    g9: LineSegment StartX=8.5 StartY=17.75 StartZ=0 EndX=7.25 EndY=17.75 EndZ=0
    g10: ArcOfCircle CenterX=7.25 CenterY=18.75 CenterZ=0 NormalX=0 NormalY=0 NormalZ=1 AngleXU=0 Radius=1 StartAngle=3.14159 EndAngle=4.71239
    g11: LineSegment StartX=6.25 StartY=18.75 StartZ=0 EndX=6.25 EndY=32.75 EndZ=0
    g12: LineSegment StartX=-6.25 StartY=32.75 StartZ=0 EndX=-5.15 EndY=32.75 EndZ=0
    g13: ArcOfCircle CenterX=-5.15 CenterY=33.75 CenterZ=0 NormalX=0 NormalY=0 NormalZ=1 AngleXU=0 Radius=1 StartAngle=4.71239 EndAngle=6.28319
    g14: LineSegment StartX=-4.15 StartY=33.75 StartZ=0 EndX=-4.15 EndY=34.25 EndZ=0
    g15: LineSegment StartX=-4.15 StartY=34.25 StartZ=0 EndX=4.15 EndY=34.25 EndZ=0
    g16: LineSegment StartX=4.15 StartY=34.25 StartZ=0 EndX=4.15 EndY=33.75 EndZ=0
    g17: ArcOfCircle CenterX=5.15 CenterY=33.75 CenterZ=0 NormalX=0 NormalY=0 NormalZ=1 AngleXU=0 Radius=1 StartAngle=3.14159 EndAngle=4.71239
    g18: LineSegment StartX=5.15 StartY=32.75 StartZ=0 EndX=6.25 EndY=32.75 EndZ=0
    g19: LineSegment StartX=-4.1 StartY=-7.25 StartZ=0 EndX=-8.5 EndY=-7.25 EndZ=0
    g20: LineSegment StartX=-8.5 StartY=-7.25 StartZ=0 EndX=-8.5 EndY=17.75 EndZ=0
    g21: LineSegment StartX=-7.25 StartY=17.75 StartZ=0 EndX=-8.5 EndY=17.75 EndZ=0
  constraints (72):
    c: Coincident(g1,g0)
    c: Diameter(g0) = 2
    c: DistanceX(g0,g0) = 0
    c: DistanceY(g0,g0) = 0
    c: Vertical(g1)
    c: Coincident(g3,g2)
    c: Vertical(g3)
    c: DistanceX(g-10,g2) = 1.5
    c: DistanceX(g2,g2) = 0
    c: DistanceY(g2,g2) = 0
    c: Diameter(g2) = 2
    c: Coincident(g4,g1)
    c: Horizontal(g4)
    c: DistanceX(g4,g-6) = 1.4
    c: DistanceX(g-8,g1) = 1.4
    c: Coincident(g5,g4)
    c: Vertical(g5)
    c: Coincident(g6,g5)
    c: Coincident(g7,g6)
    c: Horizontal(g7)
    c: Coincident(g8,g7)
    c: Vertical(g8)
    c: Coincident(g9,g8)
    c: Horizontal(g9)
    c: Coincident(g10,g9)
    c: Coincident(g11,g10)
    c: Vertical(g11)
    c: Coincident(g12,g3)
    c: Horizontal(g12)
    c: Coincident(g13,g12)
    c: Coincident(g14,g13)
    c: Vertical(g14)
    c: Coincident(g15,g14)
    c: Horizontal(g15)
    c: Coincident(g16,g15)
    c: Coincident(g17,g16)
    c: Coincident(g18,g17)
    c: Coincident(g18,g11)
    c: DistanceX(g15,g-18) = 1.5
    c: Radius(g17) = 1
    c: Horizontal(g18)
    c: Vertical(g16)
    c: DistanceX(g11,g-13) = 1.5
    c: DistanceY(g17,g-18) = 1.5
    c: Radius(g10) = 1
    c: DistanceY(g8,g-15) = 1.5
    c: DistanceX(g8,g-15) = 1.5
    c: DistanceX(g10,g9) = 0
    c: DistanceY(g10,g10) = 0
    c: Radius(g6) = 1
    c: DistanceY(g-16,g7) = 1.5
    c: DistanceX(g6,g6) = 0
    c: DistanceY(g5,g6) = 0
    c: DistanceY(g4,g-6) = 0
    c: Radius(g13) = 1
    c: DistanceX(g12,g13) = 0
    c: DistanceY(g13,g13) = 0
    c: DistanceY(g3,g-11) = 1.5
    c: DistanceX(g-17,g14) = 1.5
    c: DistanceY(g14,g-17) = 0
    c: DistanceY(g16,g17) = 0
    c: DistanceX(g17,g17) = 0
    c: Coincident(g19,g0)
    c: Horizontal(g19)
    c: Coincident(g20,g19)
    c: Vertical(g20)
    c: Coincident(g21,g2)
    c: Coincident(g21,g20)
    c: Horizontal(g21)
    c: DistanceX(g-9,g20) = 1.5
    c: DistanceY(g-8,g19) = 1.5
    c: DistanceY(g20,g-10) = 1.5
FEATURE [PartDesign::Pocket] Pocket048
  BaseFeature = -> Pad047
  Direction = (0,0,1)
  Length = 1.5
  Length2 = 5
  Profile = -> Sketch090
  ReferenceAxis = -> Sketch090 [N_Axis]
  Refine = true
  Suppressed = false
  Type = 0
FEATURE [Sketcher::SketchObject] Sketch092
  ArcFitTolerance = 1e-06
  AttachmentSupport = -> [Pocket048]
  FullyConstrained = true
  MakeInternals = false
  MapMode = 5
  Placement = pos=(0,0,-4e-16) rot=(1,0,0;3.14159rad)
  sketch-geometry (1):
    g0: Circle CenterX=0 CenterY=0 CenterZ=0 NormalX=0 NormalY=0 NormalZ=1 AngleXU=0 Radius=3.475
  constraints (2):
    c: Coincident(g0,g-1)
    c: Diameter(g0) = 6.95
FEATURE [PartDesign::Pad] Pad048
  BaseFeature = -> Pocket048
  Direction = (0,0,-1)
  Length = 1.5
  Length2 = 10
  Profile = -> Sketch092
  ReferenceAxis = -> Sketch092 [N_Axis]
  Refine = true
  Suppressed = false
  Type = 0
FEATURE [Sketcher::SketchObject] Sketch093
  ArcFitTolerance = 1e-06
  AttachmentSupport = -> [Pad048]
  FullyConstrained = true
  MakeInternals = false
  MapMode = 5
  Placement = pos=(0,0,-1.5) rot=(1,0,0;3.14159rad)
  sketch-geometry (1):
    g0: Circle CenterX=0 CenterY=0 CenterZ=0 NormalX=0 NormalY=0 NormalZ=1 AngleXU=0 Radius=2.2
  constraints (2):
    c: Coincident(g0,g-1)
    c: Diameter(g0) = 4.4
FEATURE [PartDesign::Pocket] Pocket050
  BaseFeature = -> Pad048
  Direction = (0,0,1)
  Length = 1.5
  Length2 = 5
  Profile = -> Sketch093
  ReferenceAxis = -> Sketch093 [N_Axis]
  Refine = true
  Suppressed = false
  Type = 0
FEATURE [Sketcher::SketchObject] Sketch094
  ArcFitTolerance = 1e-06
  AttachmentSupport = -> [Pocket050]
  ExternalGeometry = -> [Pocket050]
  FullyConstrained = true
  MakeInternals = false
  MapMode = 5
  Placement = pos=(0,0,-4e-16) rot=(1,0,0;3.14159rad)
  sketch-geometry (2):
    g0: Circle CenterX=0 CenterY=18.25 CenterZ=0 NormalX=0 NormalY=0 NormalZ=1 AngleXU=0 Radius=1.7
    g1: Circle CenterX=0 CenterY=30.55 CenterZ=0 NormalX=0 NormalY=0 NormalZ=1 AngleXU=0 Radius=2.2
  constraints (5):
    c: Diameter(g0) = 3.4
    c: PointOnObject(g1,g-2)
    c: Diameter(g1) = 4.4
    c: DistanceY(g1,g-3) = 10.2
    c: Coincident(g0,g-4)
FEATURE [PartDesign::Pad] Pad049
  BaseFeature = -> Pocket050
  Direction = (0,0,-1)
  Length = 4
  Length2 = 10
  Profile = -> Sketch094
  ReferenceAxis = -> Sketch094 [N_Axis]
  Refine = true
  Suppressed = false
  Type = 0
FEATURE [Sketcher::SketchObject] Sketch095
  ArcFitTolerance = 1e-06
  AttachmentSupport = -> [Pad049]
  ExternalGeometry = -> [Pad049]
  FullyConstrained = true
  MakeInternals = false
  MapMode = 5
  Placement = pos=(0,0,-4) rot=(1,0,0;3.14159rad)
  sketch-geometry (1):
    g0: Circle CenterX=0 CenterY=30.55 CenterZ=0 NormalX=0 NormalY=0 NormalZ=1 AngleXU=0 Radius=0.75
  constraints (2):
    c: Coincident(g0,g-3)
    c: Diameter(g0) = 1.5
FEATURE [PartDesign::Pocket] Pocket051
  BaseFeature = -> Pad049
  Direction = (0,0,1)
  Length = 4
  Length2 = 5
  Profile = -> Sketch095
  ReferenceAxis = -> Sketch095 [N_Axis]
  Refine = true
  Suppressed = false
  Type = 0
FEATURE [Sketcher::SketchObject] Sketch096
  ArcFitTolerance = 1e-06
  AttachmentSupport = -> [Pocket051]
  ExternalGeometry = -> [Pocket051]
  FullyConstrained = true
  MakeInternals = false
  MapMode = 5
  Placement = pos=(0,0,-4e-16) rot=(1,0,0;3.14159rad)
  sketch-geometry (16):
    g0: ArcOfCircle CenterX=-3 CenterY=18.25 CenterZ=0 NormalX=0 NormalY=0 NormalZ=1 AngleXU=0 Radius=0.7 StartAngle=4.71239 EndAngle=7.85398
    g1: ArcOfCircle CenterX=-5 CenterY=18.25 CenterZ=0 NormalX=0 NormalY=0 NormalZ=1 AngleXU=0 Radius=0.7 StartAngle=1.5708 EndAngle=4.71239
    g2: LineSegment StartX=-3 StartY=17.55 StartZ=0 EndX=-5 EndY=17.55 EndZ=0
    g3: LineSegment StartX=-3 StartY=18.95 StartZ=0 EndX=-5 EndY=18.95 EndZ=0
    g4: ArcOfCircle CenterX=3 CenterY=18.25 CenterZ=0 NormalX=0 NormalY=0 NormalZ=1 AngleXU=0 Radius=0.7 StartAngle=1.5708 EndAngle=4.71239
    g5: ArcOfCircle CenterX=5 CenterY=18.25 CenterZ=0 NormalX=0 NormalY=0 NormalZ=1 AngleXU=0 Radius=0.7 StartAngle=4.71239 EndAngle=7.85398
    g6: LineSegment StartX=3 StartY=18.95 StartZ=0 EndX=5 EndY=18.95 EndZ=0
    g7: LineSegment StartX=3 StartY=17.55 StartZ=0 EndX=5 EndY=17.55 EndZ=0
    g8: ArcOfCircle CenterX=0 CenterY=21.25 CenterZ=0 NormalX=0 NormalY=0 NormalZ=1 AngleXU=0 Radius=0.7 StartAngle=3.14159 EndAngle=6.28319
    g9: ArcOfCircle CenterX=0 CenterY=23.25 CenterZ=0 NormalX=0 NormalY=0 NormalZ=1 AngleXU=0 Radius=0.7 StartAngle=5e-16 EndAngle=3.14159
    g10: LineSegment StartX=-0.7 StartY=21.25 StartZ=0 EndX=-0.7 EndY=23.25 EndZ=0
    g11: LineSegment StartX=0.7 StartY=21.25 StartZ=0 EndX=0.7 EndY=23.25 EndZ=0
    g12: ArcOfCircle CenterX=0 CenterY=15.25 CenterZ=0 NormalX=0 NormalY=0 NormalZ=1 AngleXU=0 Radius=0.7 StartAngle=-9e-16 EndAngle=3.14159
    g13: ArcOfCircle CenterX=0 CenterY=13.25 CenterZ=0 NormalX=0 NormalY=0 NormalZ=1 AngleXU=0 Radius=0.7 StartAngle=3.14159 EndAngle=6.28319
    g14: LineSegment StartX=0.7 StartY=15.25 StartZ=0 EndX=0.7 EndY=13.25 EndZ=0
    g15: LineSegment StartX=-0.7 StartY=15.25 StartZ=0 EndX=-0.7 EndY=13.25 EndZ=0
  constraints (40):
    c: Tangent(g0,g2) = 1.5708
    c: Tangent(g0,g3) = -1.5708
    c: Tangent(g1,g2) = 1.5708
    c: Tangent(g1,g3) = -1.5708
    c: Equal(g0,g1)
    c: Horizontal(g3)
    c: Tangent(g4,g6) = 1.5708
    c: Tangent(g4,g7) = -1.5708
    c: Tangent(g5,g6) = 1.5708
    c: Tangent(g5,g7) = -1.5708
    c: Equal(g4,g5)
    c: Horizontal(g7)
    c: Tangent(g8,g10) = 1.5708
    c: Tangent(g8,g11) = -1.5708
    c: Tangent(g9,g10) = 1.5708
    c: Tangent(g9,g11) = -1.5708
    c: Equal(g8,g9)
    c: Vertical(g11)
    c: PointOnObject(g8,g-2)
    c: Tangent(g12,g14) = 1.5708
    c: Tangent(g12,g15) = -1.5708
    c: Tangent(g13,g14) = 1.5708
    c: Tangent(g13,g15) = -1.5708
    c: Equal(g12,g13)
    c: Vertical(g15)
    c: Diameter(g1) = 1.4
    c: Diameter(g8) = 1.4
    c: Diameter(g4) = 1.4
    c: Diameter(g12) = 1.4
    c: Distance(g12,g13) = 2
    c: Distance(g0,g1) = 2
    c: Distance(g8,g9) = 2
    c: Distance(g4,g5) = 2
    c: DistanceX(g0,g-3) = 3
    c: DistanceX(g-3,g4) = 3
    c: DistanceY(g12,g-3) = 3
    c: DistanceY(g-3,g8) = 3
    c: PointOnObject(g12,g-2)
    c: DistanceY(g0,g-3) = 0
    c: DistanceY(g4,g-3) = 0
FEATURE [PartDesign::Pad] Pad050
  BaseFeature = -> Pocket051
  Direction = (0,0,-1)
  Length = 0.4
  Length2 = 10
  Profile = -> Sketch096
  ReferenceAxis = -> Sketch096 [N_Axis]
  Refine = true
  Suppressed = false
  Type = 0
FEATURE [Sketcher::SketchObject] Sketch097
  ArcFitTolerance = 1e-06
  AttachmentSupport = -> [Pad050]
  FullyConstrained = true
  MakeInternals = false
  MapMode = 5
  Placement = pos=(5.65,0,-4.7e-15) rot=(0.57735,0.57735,0.57735;2.0944rad)
  sketch-geometry (1):
    g0: Circle CenterX=-37.25 CenterY=-1.5 CenterZ=0 NormalX=0 NormalY=0 NormalZ=1 AngleXU=0 Radius=1.5
  constraints (3):
    c: Diameter(g0) = 3
    c: PointOnObject(g0,g-3)
    c: DistanceX(g0,g-3) = 2.5
FEATURE [PartDesign::Pocket] Pocket052
  BaseFeature = -> Pad050
  Direction = (-1,0,0)
  Length = 12
  Length2 = 5
  Profile = -> Sketch097
  ReferenceAxis = -> Sketch097 [N_Axis]
  Refine = true
  Suppressed = false
  Type = 0
FEATURE [Sketcher::SketchObject] Sketch098
  ArcFitTolerance = 1e-06
  AttachmentSupport = -> [Pocket052]
  ExternalGeometry = -> [Pocket052]
  FullyConstrained = true
  MakeInternals = false
  MapMode = 5
  Placement = pos=(7.75,0,0) rot=(0.57735,0.57735,0.57735;2.0944rad)
  sketch-geometry (1):
    g0: Circle CenterX=-26.65 CenterY=-1.5 CenterZ=0 NormalX=0 NormalY=0 NormalZ=1 AngleXU=0 Radius=1.5
  constraints (3):
    c: Tangent(g0,g-1)
    c: DistanceX(g-3,g0) = 6.6
    c: PointOnObject(g0,g-3)
FEATURE [PartDesign::Pocket] Pocket053
  BaseFeature = -> Pocket052
  Direction = (-1,0,0)
  Length = 16
  Length2 = 5
  Profile = -> Sketch098
  ReferenceAxis = -> Sketch098 [N_Axis]
  Refine = true
  Suppressed = false
  Type = 0
FEATURE [Sketcher::SketchObject] Sketch099
  ArcFitTolerance = 1e-06
  AttachmentSupport = -> [Pocket053]
  FullyConstrained = true
  MakeInternals = false
  MapMode = 5
  Placement = pos=(7.75,0,0) rot=(0.57735,0.57735,0.57735;2.0944rad)
  sketch-geometry (4):
    g0: LineSegment StartX=-24.75 StartY=1.7 StartZ=0 EndX=-24.75 EndY=-1.5 EndZ=0
    g1: LineSegment StartX=-24.75 StartY=-1.5 StartZ=0 EndX=-21.5 EndY=-1.5 EndZ=0
    g2: LineSegment StartX=-21.5 StartY=-1.5 StartZ=0 EndX=-21.5 EndY=1.7 EndZ=0
    g3: LineSegment StartX=-21.5 StartY=1.7 StartZ=0 EndX=-24.75 EndY=1.7 EndZ=0
  constraints (12):
    c: Coincident(g0,g1)
    c: Coincident(g1,g2)
    c: Coincident(g2,g3)
    c: Coincident(g3,g0)
    c: Vertical(g0)
    c: Vertical(g2)
    c: Horizontal(g1)
    c: Horizontal(g3)
    c: PointOnObject(g0,g-3)
    c: PointOnObject(g1,g-4)
    c: DistanceX(g0,g2) = 3.25
    c: DistanceX(g2,g-3) = 2.25
FEATURE [PartDesign::Pad] Pad051
  BaseFeature = -> Pocket053
  Direction = (1,0,0)
  Length = 0.2
  Length2 = 10
  Profile = -> Sketch099
  ReferenceAxis = -> Sketch099 [N_Axis]
  Refine = true
  Suppressed = false
  Type = 0
FEATURE [PartDesign::Body] Body009  label="Front_Torso"
  AllowCompound = false
  Group = -> [Sketch080,Pad042,DatumPlane012,Sketch081,Pad043,DatumPlane013,Sketch082,Pocket044,Sketch083,Pocket045,Sketch084,Pocket046,Sketch085,Pad044,Sketch086,Pad045,DatumPlane014,Sketch087,Pocket047,Sketch088,Pad046,Sketch089,Pad047,Sketch090,Pocket048,Sketch092,Pad048,Sketch093,Pocket050,Sketch094,Pad049,Sketch095,Pocket051,Sketch096,Pad050,Sketch097,Pocket052,Sketch098,Pocket053,Sketch099,Pad051,+24 more]
  Origin = -> Origin010
  Placement = pos=(38.2,-13.75,1.5) rot=(0,0,1;0rad)
  Tip = -> Pocket169
COMPONENT P2 — recipe-attached ("Chest", modeled in this document).
Construction recipe (the document's own serialized feature program — sketch geometry with constraints, then the solid features built on it; lengths are millimeters unless a unit is written):

FEATURE [Sketcher::SketchObject] Sketch102
  ArcFitTolerance = 1e-06
  AttachmentSupport = -> [YZ_Plane012]
  FullyConstrained = true
  MakeInternals = false
  MapMode = 5
  Placement = pos=(0,0,0) rot=(0.57735,0.57735,0.57735;2.0944rad)
  sketch-geometry (4):
    g0: LineSegment StartX=12.8 StartY=0 StartZ=0 EndX=12.8 EndY=12.1 EndZ=0
    g1: LineSegment StartX=12.8 StartY=12.1 StartZ=0 EndX=0 EndY=12.1 EndZ=0
    g2: LineSegment StartX=0 StartY=12.1 StartZ=0 EndX=0 EndY=0 EndZ=0
    g3: LineSegment StartX=0 StartY=0 StartZ=0 EndX=12.8 EndY=0 EndZ=0
  constraints (12):
    c: Coincident(g0,g1)
    c: Coincident(g1,g2)
    c: Coincident(g2,g3)
    c: Coincident(g3,g0)
    c: Vertical(g0)
    c: Vertical(g2)
    c: Horizontal(g1)
    c: Horizontal(g3)
    c: PointOnObject(g0,g-1)
    c: PointOnObject(g1,g-2)
    c: DistanceX(g1,g0) = 12.8
    c: DistanceY(g2,g1) = 12.1
FEATURE [PartDesign::Pad] Pad053
  Direction = (1,0,0)
  Length = 20
  Length2 = 10
  Placement = pos=(0,0,0) rot=(1,1,1;2.0944rad)
  Profile = -> Sketch102
  ReferenceAxis = -> Sketch102 [N_Axis]
  Refine = true
  Suppressed = false
  Type = 0
FEATURE [Sketcher::SketchObject] Sketch104
  ArcFitTolerance = 1e-06
  AttachmentSupport = -> [Pad053]
  ExternalGeometry = -> [Pad053]
  FullyConstrained = true
  MakeInternals = false
  MapMode = 5
  Placement = pos=(0,2.7e-15,12.1) rot=(0,0,-1;1.5708rad)
  sketch-geometry (4):
    g0: LineSegment StartX=0 StartY=14.05 StartZ=0 EndX=-4.75 EndY=14.05 EndZ=0
    g1: LineSegment StartX=-4.75 StartY=14.05 StartZ=0 EndX=-4.75 EndY=5.95 EndZ=0
    g2: LineSegment StartX=-4.75 StartY=5.95 StartZ=0 EndX=0 EndY=5.95 EndZ=0
    g3: LineSegment StartX=0 StartY=5.95 StartZ=0 EndX=0 EndY=14.05 EndZ=0
  constraints (12):
    c: Coincident(g0,g1)
    c: Coincident(g1,g2)
    c: Coincident(g2,g3)
    c: Coincident(g3,g0)
    c: Horizontal(g0)
    c: Horizontal(g2)
    c: Vertical(g1)
    c: Vertical(g3)
    c: PointOnObject(g0,g-2)
    c: DistanceX(g0,g0) = 4.75
    c: DistanceY(g1,g1) = 8.1
    c: DistanceY(g0,g-3) = 5.95
FEATURE [PartDesign::Pocket] Pocket055
  BaseFeature = -> Pad053
  Direction = (0,0,-1)
  Length = 13
  Length2 = 5
  Placement = pos=(0,0,0) rot=(1,1,1;2.0944rad)
  Profile = -> Sketch104
  ReferenceAxis = -> Sketch104 [N_Axis]
  Refine = true
  Suppressed = false
  Type = 0
FEATURE [Sketcher::SketchObject] Sketch105
  ArcFitTolerance = 1e-06
  AttachmentSupport = -> [Pocket055]
  ExternalGeometry = -> [Pocket055]
  FullyConstrained = true
  MakeInternals = false
  MapMode = 5
  Placement = pos=(0,2.7e-15,12.1) rot=(0,0,-1;1.5708rad)
  sketch-geometry (4):
    g0: LineSegment StartX=-12.8 StartY=12.3 StartZ=0 EndX=-12.8 EndY=7.7 EndZ=0
    g1: LineSegment StartX=-12.8 StartY=7.7 StartZ=0 EndX=-6.2 EndY=7.7 EndZ=0
    g2: LineSegment StartX=-6.2 StartY=7.7 StartZ=0 EndX=-6.2 EndY=12.3 EndZ=0
    g3: LineSegment StartX=-6.2 StartY=12.3 StartZ=0 EndX=-12.8 EndY=12.3 EndZ=0
  constraints (12):
    c: Coincident(g0,g1)
    c: Coincident(g1,g2)
    c: Coincident(g2,g3)
    c: Coincident(g3,g0)
    c: Vertical(g0)
    c: Vertical(g2)
    c: Horizontal(g1)
    c: Horizontal(g3)
    c: PointOnObject(g0,g-3)
    c: DistanceY(g2,g2) = 4.6
    c: DistanceX(g3,g3) = 6.6
    c: DistanceY(g0,g-3) = 7.7
FEATURE [PartDesign::Pocket] Pocket056
  BaseFeature = -> Pocket055
  Direction = (0,0,-1)
  Length = 7.1
  Length2 = 5
  Placement = pos=(0,0,0) rot=(1,1,1;2.0944rad)
  Profile = -> Sketch105
  ReferenceAxis = -> Sketch105 [N_Axis]
  Refine = true
  Suppressed = false
  Type = 0
FEATURE [Sketcher::SketchObject] Sketch106
  ArcFitTolerance = 1e-06
  AttachmentSupport = -> [Pocket056]
  ExternalGeometry = -> [Pocket056]
  FullyConstrained = true
  MakeInternals = false
  MapMode = 5
  Placement = pos=(0,2.7e-15,12.1) rot=(0,0,-1;1.5708rad)
  sketch-geometry (16):
    g0: LineSegment StartX=-12.8 StartY=20 StartZ=0 EndX=-12.8 EndY=14 EndZ=0
    g1: LineSegment StartX=-12.8 StartY=14 StartZ=0 EndX=-6.2 EndY=14 EndZ=0
    g2: LineSegment StartX=-6.2 StartY=14 StartZ=0 EndX=-6.2 EndY=20 EndZ=0
    g3: LineSegment StartX=-6.2 StartY=20 StartZ=0 EndX=-12.8 EndY=20 EndZ=0
    g4: LineSegment StartX=-12.8 StartY=0 StartZ=0 EndX=-6.2 EndY=0 EndZ=0
    g5: LineSegment StartX=-6.2 StartY=0 StartZ=0 EndX=-6.2 EndY=6 EndZ=0
    g6: LineSegment StartX=-6.2 StartY=6 StartZ=0 EndX=-12.8 EndY=6 EndZ=0
    g7: LineSegment StartX=-12.8 StartY=6 StartZ=0 EndX=-12.8 EndY=0 EndZ=0
    g8: LineSegment StartX=0 StartY=15.8 StartZ=0 EndX=0 EndY=20 EndZ=0
    g9: LineSegment StartX=0 StartY=20 StartZ=0 EndX=-4.75 EndY=20 EndZ=0
    g10: LineSegment StartX=-4.75 StartY=20 StartZ=0 EndX=-4.75 EndY=15.8 EndZ=0
    g11: LineSegment StartX=-4.75 StartY=15.8 StartZ=0 EndX=0 EndY=15.8 EndZ=0
    g12: LineSegment StartX=0 StartY=0 StartZ=0 EndX=0 EndY=4.2 EndZ=0
    g13: LineSegment StartX=0 StartY=4.2 StartZ=0 EndX=-4.75 EndY=4.2 EndZ=0
    g14: LineSegment StartX=-4.75 StartY=4.2 StartZ=0 EndX=-4.75 EndY=0 EndZ=0
    g15: LineSegment StartX=-4.75 StartY=0 StartZ=0 EndX=0 EndY=0 EndZ=0
  constraints (45):
    c: Coincident(g0,g1)
    c: Coincident(g1,g2)
    c: Coincident(g2,g3)
    c: Coincident(g3,g0)
    c: Vertical(g0)
    c: Vertical(g2)
    c: Horizontal(g1)
    c: Horizontal(g3)
    c: Coincident(g0,g-6)
    c: Coincident(g4,g5)
    c: Coincident(g5,g6)
    c: Coincident(g6,g7)
    c: Coincident(g7,g4)
    c: Horizontal(g4)
    c: Horizontal(g6)
    c: Vertical(g5)
    c: Vertical(g7)
    c: Coincident(g4,g-5)
    c: DistanceY(g2,g2) = 6
    c: DistanceY(g5,g5) = 6
    c: DistanceX(g1,g1) = 6.6
    c: DistanceX(g6,g6) = 6.6
    c: Coincident(g8,g9)
    c: Coincident(g9,g10)
    c: Coincident(g10,g11)
    c: Coincident(g11,g8)
    c: Vertical(g8)
    c: Vertical(g10)
    c: Horizontal(g9)
    c: Horizontal(g11)
    c: PointOnObject(g8,g-2)
    c: PointOnObject(g9,g-3)
    c: Coincident(g12,g13)
    c: Coincident(g13,g14)
    c: Coincident(g14,g15)
    c: Coincident(g15,g12)
    c: Vertical(g12)
    c: Vertical(g14)
    c: Horizontal(g13)
    c: Horizontal(g15)
    c: Coincident(g12,g-1)
    c: DistanceX(g11,g11) = 4.75
    c: DistanceX(g13,g13) = 4.75
    c: DistanceY(g10,g10) = 4.2
    c: DistanceY(g14,g14) = 4.2
FEATURE [PartDesign::Pocket] Pocket057
  BaseFeature = -> Pocket056
  Direction = (0,0,-1)
  Length = 1
  Length2 = 5
  Placement = pos=(0,0,0) rot=(1,1,1;2.0944rad)
  Profile = -> Sketch106
  ReferenceAxis = -> Sketch106 [N_Axis]
  Refine = true
  Suppressed = false
  Type = 0
FEATURE [Sketcher::SketchObject] Sketch107
  ArcFitTolerance = 1e-06
  AttachmentSupport = -> [Pocket057]
  ExternalGeometry = -> [Pocket057]
  FullyConstrained = true
  MakeInternals = false
  MapMode = 5
  Placement = pos=(20,0,0) rot=(0.57735,0.57735,0.57735;2.0944rad)
  sketch-geometry (3):
    g0: LineSegment StartX=1.75 StartY=11.1 StartZ=0 EndX=0 EndY=3.6 EndZ=0
    g1: LineSegment StartX=0 StartY=3.6 StartZ=0 EndX=0 EndY=11.1 EndZ=0
    g2: LineSegment StartX=1.75 StartY=11.1 StartZ=0 EndX=0 EndY=11.1 EndZ=0
  constraints (8):
    c: PointOnObject(g0,g-3)
    c: PointOnObject(g0,g-2)
    c: Coincident(g1,g0)
    c: Coincident(g1,g-3)
    c: Coincident(g2,g0)
    c: Coincident(g2,g1)
    c: DistanceX(g0,g-3) = 3
    c: DistanceY(g0,g1) = 7.5
FEATURE [PartDesign::Pocket] Pocket058
  BaseFeature = -> Pocket057
  Direction = (-1,0,0)
  Length = 4.2
  Length2 = 5
  Placement = pos=(0,0,0) rot=(1,1,1;2.0944rad)
  Profile = -> Sketch107
  ReferenceAxis = -> Sketch107 [N_Axis]
  Refine = true
  Suppressed = false
  Type = 0
FEATURE [Sketcher::SketchObject] Sketch108
  ArcFitTolerance = 1e-06
  AttachmentSupport = -> [Pocket058]
  ExternalGeometry = -> [Pocket058]
  FullyConstrained = true
  MakeInternals = false
  MapMode = 5
  Placement = pos=(0,0,0) rot=(0.57735,0.57735,-0.57735;4.18879rad)
  sketch-geometry (3):
    g0: LineSegment StartX=1.75 StartY=-11.1 StartZ=0 EndX=0 EndY=-11.1 EndZ=0
    g1: LineSegment StartX=1.75 StartY=-11.1 StartZ=0 EndX=0 EndY=-3.6 EndZ=0
    g2: LineSegment StartX=0 StartY=-3.6 StartZ=0 EndX=0 EndY=-11.1 EndZ=0
  constraints (8):
    c: Coincident(g0,g-3)
    c: Coincident(g1,g0)
    c: PointOnObject(g1,g-2)
    c: Coincident(g2,g1)
    c: Coincident(g2,g0)
    c: DistanceX(g0,g-3) = 3
    c: DistanceY(g0,g1) = 7.5
    c: PointOnObject(g0,g-3)
FEATURE [PartDesign::Pocket] Pocket059
  BaseFeature = -> Pocket058
  Direction = (1,-1e-15,1e-16)
  Length = 4.2
  Length2 = 5
  Placement = pos=(0,0,0) rot=(1,1,1;2.0944rad)
  Profile = -> Sketch108
  ReferenceAxis = -> Sketch108 [N_Axis]
  Refine = true
  Suppressed = false
  Type = 0
FEATURE [Sketcher::SketchObject] Sketch109
  ArcFitTolerance = 1e-06
  AttachmentSupport = -> [Pocket059]
  ExternalGeometry = -> [Pocket059]
  FullyConstrained = true
  MakeInternals = false
  MapMode = 5
  Placement = pos=(0,0,11.1) rot=(0,0,-1;1.5708rad)
  sketch-geometry (2):
    g0: Circle CenterX=-10 CenterY=17.05 CenterZ=0 NormalX=0 NormalY=0 NormalZ=1 AngleXU=0 Radius=1.4
    g1: Circle CenterX=-10 CenterY=2.95 CenterZ=0 NormalX=0 NormalY=0 NormalZ=1 AngleXU=0 Radius=1.4
  constraints (6):
    c: DistanceX(g-6,g1) = 2.8
    c: DistanceX(g-4,g0) = 2.8
    c: DistanceY(g-6,g1) = 2.95
    c: Diameter(g1) = 2.8
    c: Diameter(g0) = 2.8
    c: DistanceY(g0,g-4) = 2.95
FEATURE [PartDesign::Pad] Pad054
  BaseFeature = -> Pocket059
  Direction = (0,0,1)
  Length = 1
  Length2 = 10
  Placement = pos=(0,0,0) rot=(1,1,1;2.0944rad)
  Profile = -> Sketch109
  ReferenceAxis = -> Sketch109 [N_Axis]
  Refine = true
  Suppressed = false
  Type = 0
FEATURE [PartDesign::Fillet] Fillet030
  Base = -> Pad054 [Edge72,Edge83]
  BaseFeature = -> Pad054
  Placement = pos=(0,0,0) rot=(1,1,1;2.0944rad)
  Radius = 0.9
  Refine = true
  SupportTransform = false
  Suppressed = false
  UseAllEdges = false
FEATURE [Sketcher::SketchObject] Sketch110
  ArcFitTolerance = 1e-06
  AttachmentSupport = -> [Fillet030]
  ExternalGeometry = -> [Fillet030]
  FullyConstrained = true
  MakeInternals = false
  MapMode = 5
  Placement = pos=(0,6.2,0) rot=(0.57735,0.57735,0.57735;4.18879rad)
  sketch-geometry (4):
    g0: LineSegment StartX=5 StartY=12.3 StartZ=0 EndX=5 EndY=7.7 EndZ=0
    g1: LineSegment StartX=5 StartY=7.7 StartZ=0 EndX=9.85 EndY=7.7 EndZ=0
    g2: LineSegment StartX=9.85 StartY=7.7 StartZ=0 EndX=9.85 EndY=12.3 EndZ=0
    g3: LineSegment StartX=9.85 StartY=12.3 StartZ=0 EndX=5 EndY=12.3 EndZ=0
  constraints (11):
    c: Coincident(g0,g1)
    c: Coincident(g1,g2)
    c: Coincident(g2,g3)
    c: Coincident(g3,g0)
    c: Vertical(g0)
    c: Vertical(g2)
    c: Horizontal(g1)
    c: Horizontal(g3)
    c: Coincident(g0,g-4)
    c: PointOnObject(g1,g-5)
    c: DistanceX(g2,g-3) = 2.25
FEATURE [PartDesign::Pad] Pad055
  BaseFeature = -> Fillet030
  Direction = (0,1,-1.3e-15)
  Length = 0.5
  Length2 = 10
  Placement = pos=(0,0,0) rot=(1,1,1;2.0944rad)
  Profile = -> Sketch110
  ReferenceAxis = -> Sketch110 [N_Axis]
  Refine = true
  Suppressed = false
  Type = 0
FEATURE [Sketcher::SketchObject] Sketch111
  ArcFitTolerance = 1e-06
  AttachmentSupport = -> [Pad055]
  ExternalGeometry = -> [Pad055]
  FullyConstrained = false
  MakeInternals = false
  MapMode = 5
  Placement = pos=(0,6.7,-8.6e-15) rot=(0.57735,0.57735,0.57735;4.18879rad)
  sketch-geometry (4):
    g0: LineSegment StartX=5 StartY=12.3 StartZ=0 EndX=5 EndY=7.6 EndZ=0
    g1: LineSegment StartX=5 StartY=7.6 StartZ=0 EndX=7.4 EndY=7.6 EndZ=0
    g2: LineSegment StartX=7.4 StartY=7.6 StartZ=0 EndX=7.4 EndY=12.3 EndZ=0
    g3: LineSegment StartX=7.4 StartY=12.3 StartZ=0 EndX=5 EndY=12.3 EndZ=0
  constraints (10):
    c: Coincident(g0,g1)
    c: Coincident(g1,g2)
    c: Coincident(g2,g3)
    c: Coincident(g3,g0)
    c: Vertical(g0)
    c: Vertical(g2)
    c: Horizontal(g1)
    c: Horizontal(g3)
    c: Coincident(g0,g-4)
    c: DistanceX(g2,g-3) = 4.7
FEATURE [PartDesign::Pad] Pad056
  BaseFeature = -> Pad055
  Direction = (-1e-16,1,-1.4e-15)
  Length = 0.5
  Length2 = 10
  Placement = pos=(0,0,0) rot=(1,1,1;2.0944rad)
  Profile = -> Sketch111
  ReferenceAxis = -> Sketch111 [N_Axis]
  Refine = true
  Suppressed = false
  Type = 0
FEATURE [Sketcher::SketchObject] Sketch112
  ArcFitTolerance = 1e-06
  AttachmentSupport = -> [Pad056]
  ExternalGeometry = -> [Pad056]
  FullyConstrained = true
  MakeInternals = false
  MapMode = 5
  Placement = pos=(0,0,0) rot=(0.707107,0.707107,0;3.14159rad)
  sketch-geometry (8):
    g0: LineSegment StartX=1.5 StartY=18.5 StartZ=0 EndX=1.5 EndY=15.5 EndZ=0
    g1: LineSegment StartX=1.5 StartY=15.5 StartZ=0 EndX=11.3 EndY=15.5 EndZ=0
    g2: LineSegment StartX=11.3 StartY=15.5 StartZ=0 EndX=11.3 EndY=18.5 EndZ=0
    g3: LineSegment StartX=11.3 StartY=18.5 StartZ=0 EndX=1.5 EndY=18.5 EndZ=0
    g4: LineSegment StartX=1.5 StartY=4.5 StartZ=0 EndX=1.5 EndY=1.5 EndZ=0
    g5: LineSegment StartX=1.5 StartY=1.5 StartZ=0 EndX=11.3 EndY=1.5 EndZ=0
    g6: LineSegment StartX=11.3 StartY=1.5 StartZ=0 EndX=11.3 EndY=4.5 EndZ=0
    g7: LineSegment StartX=11.3 StartY=4.5 StartZ=0 EndX=1.5 EndY=4.5 EndZ=0
  constraints (24):
    c: Coincident(g0,g1)
    c: Coincident(g1,g2)
    c: Coincident(g2,g3)
    c: Coincident(g3,g0)
    c: Vertical(g0)
    c: Vertical(g2)
    c: Horizontal(g1)
    c: Horizontal(g3)
    c: Coincident(g4,g5)
    c: Coincident(g5,g6)
    c: Coincident(g6,g7)
    c: Coincident(g7,g4)
    c: Vertical(g4)
    c: Vertical(g6)
    c: Horizontal(g5)
    c: Horizontal(g7)
    c: DistanceX(g-6,g4) = 1.5
    c: DistanceX(g5,g-4) = 1.5
    c: DistanceX(g-3,g0) = 1.5
    c: DistanceX(g2,g-4) = 1.5
    c: DistanceY(g-5,g0) = 1.45
    c: DistanceY(g2,g-4) = 1.5
    c: DistanceY(g-4,g5) = 1.5
    c: DistanceY(g4,g-6) = 1.45
FEATURE [PartDesign::Pocket] Pocket060
  BaseFeature = -> Pad056
  Direction = (-2.8e-15,1.2e-15,1)
  Length = 9.6
  Length2 = 5
  Placement = pos=(0,0,0) rot=(1,1,1;2.0944rad)
  Profile = -> Sketch112
  ReferenceAxis = -> Sketch112 [N_Axis]
  Refine = true
  Suppressed = false
  Type = 0
FEATURE [Sketcher::SketchObject] Sketch113
  ArcFitTolerance = 1e-06
  AttachmentSupport = -> [Pocket060]
  ExternalGeometry = -> [Pocket060]
  FullyConstrained = true
  MakeInternals = false
  MapMode = 5
  Placement = pos=(0,0,0) rot=(0.707107,0.707107,0;3.14159rad)
  sketch-geometry (8):
    g0: LineSegment StartX=4.75 StartY=5.95 StartZ=0 EndX=4.75 EndY=0 EndZ=0
    g1: LineSegment StartX=4.75 StartY=0 StartZ=0 EndX=12.8 EndY=0 EndZ=0
    g2: LineSegment StartX=12.8 StartY=0 StartZ=0 EndX=12.8 EndY=5.95 EndZ=0
    g3: LineSegment StartX=12.8 StartY=5.95 StartZ=0 EndX=4.75 EndY=5.95 EndZ=0
    g4: LineSegment StartX=4.75 StartY=14.05 StartZ=0 EndX=12.8 EndY=14.05 EndZ=0
    g5: LineSegment StartX=12.8 StartY=14.05 StartZ=0 EndX=12.8 EndY=20 EndZ=0
    g6: LineSegment StartX=12.8 StartY=20 StartZ=0 EndX=4.75 EndY=20 EndZ=0
    g7: LineSegment StartX=4.75 StartY=20 StartZ=0 EndX=4.75 EndY=14.05 EndZ=0
  constraints (20):
    c: Coincident(g0,g1)
    c: Coincident(g1,g2)
    c: Coincident(g2,g3)
    c: Coincident(g3,g0)
    c: Vertical(g0)
    c: Vertical(g2)
    c: Horizontal(g1)
    c: Horizontal(g3)
    c: Coincident(g0,g-5)
    c: Coincident(g1,g-4)
    c: Coincident(g4,g5)
    c: Coincident(g5,g6)
    c: Coincident(g6,g7)
    c: Coincident(g7,g4)
    c: Horizontal(g4)
    c: Horizontal(g6)
    c: Vertical(g5)
    c: Vertical(g7)
    c: Coincident(g4,g-6)
    c: Coincident(g5,g-4)
FEATURE [PartDesign::Pocket] Pocket061
  BaseFeature = -> Pocket060
  Direction = (-3.1e-15,1.3e-15,1)
  Length = 8.1
  Length2 = 5
  Placement = pos=(0,0,0) rot=(1,1,1;2.0944rad)
  Profile = -> Sketch113
  ReferenceAxis = -> Sketch113 [N_Axis]
  Refine = true
  Suppressed = false
  Type = 0
FEATURE [Sketcher::SketchObject] Sketch114
  ArcFitTolerance = 1e-06
  AttachmentSupport = -> [Pocket061]
  ExternalGeometry = -> [Pocket061]
  FullyConstrained = true
  MakeInternals = false
  MapMode = 5
  Placement = pos=(0,0,0) rot=(0.707107,0.707107,0;3.14159rad)
  sketch-geometry (4):
    g0: LineSegment StartX=4.75 StartY=14.05 StartZ=0 EndX=4.75 EndY=5.95 EndZ=0
    g1: LineSegment StartX=4.75 StartY=5.95 StartZ=0 EndX=11.3 EndY=5.95 EndZ=0
    g2: LineSegment StartX=11.3 StartY=5.95 StartZ=0 EndX=11.3 EndY=14.05 EndZ=0
    g3: LineSegment StartX=11.3 StartY=14.05 StartZ=0 EndX=4.75 EndY=14.05 EndZ=0
  constraints (11):
    c: Coincident(g0,g1)
    c: Coincident(g1,g2)
    c: Coincident(g2,g3)
    c: Coincident(g3,g0)
    c: Vertical(g0)
    c: Vertical(g2)
    c: Horizontal(g1)
    c: Horizontal(g3)
    c: Coincident(g0,g-3)
    c: PointOnObject(g1,g-4)
    c: DistanceX(g2,g-3) = 1.5
FEATURE [PartDesign::Pocket] Pocket062
  BaseFeature = -> Pocket061
  Direction = (-3.4e-15,1.4e-15,1)
  Length = 3.5
  Length2 = 5
  Placement = pos=(0,0,0) rot=(1,1,1;2.0944rad)
  Profile = -> Sketch114
  ReferenceAxis = -> Sketch114 [N_Axis]
  Refine = true
  Suppressed = false
  Type = 0
FEATURE [Sketcher::SketchObject] Sketch115
  ArcFitTolerance = 1e-06
  AttachmentSupport = -> [Pocket062]
  ExternalGeometry = -> [Pocket062]
  FullyConstrained = true
  MakeInternals = false
  MapMode = 5
  Placement = pos=(0,4.75,0) rot=(0.57735,0.57735,-0.57735;2.0944rad)
  sketch-geometry (4):
    g0: LineSegment StartX=-3.5 StartY=14.05 StartZ=0 EndX=-9.4 EndY=14.05 EndZ=0
    g1: LineSegment StartX=-9.4 StartY=14.05 StartZ=0 EndX=-9.4 EndY=5.95 EndZ=0
    g2: LineSegment StartX=-9.4 StartY=5.95 StartZ=0 EndX=-3.5 EndY=5.95 EndZ=0
    g3: LineSegment StartX=-3.5 StartY=5.95 StartZ=0 EndX=-3.5 EndY=14.05 EndZ=0
  constraints (10):
    c: Coincident(g0,g1)
    c: Coincident(g1,g2)
    c: Coincident(g2,g3)
    c: Coincident(g3,g0)
    c: Horizontal(g0)
    c: Horizontal(g2)
    c: Vertical(g1)
    c: Coincident(g0,g-3)
    c: Coincident(g2,g-3)
    c: DistanceX(g-4,g0) = 2.7
FEATURE [PartDesign::Pocket] Pocket063
  BaseFeature = -> Pocket062
  Direction = (1e-16,1,-3.2e-15)
  Length = 0.9
  Length2 = 5
  Placement = pos=(0,0,0) rot=(1,1,1;2.0944rad)
  Profile = -> Sketch115
  ReferenceAxis = -> Sketch115 [N_Axis]
  Refine = true
  Suppressed = false
  Type = 0
FEATURE [Sketcher::SketchObject] Sketch116
  ArcFitTolerance = 1e-06
  AttachmentSupport = -> [Pocket063]
  ExternalGeometry = -> [Pocket063]
  FullyConstrained = true
  MakeInternals = false
  MapMode = 5
  Placement = pos=(-2.67e-14,1.17e-14,9.6) rot=(0.707107,0.707107,0;3.14159rad)
  sketch-geometry (2):
    g0: Circle CenterX=10 CenterY=17.05 CenterZ=0 NormalX=0 NormalY=0 NormalZ=1 AngleXU=0 Radius=1.3
    g1: Circle CenterX=10 CenterY=2.95 CenterZ=0 NormalX=0 NormalY=0 NormalZ=1 AngleXU=0 Radius=1.3
  constraints (6):
    c: Tangent(g0,g-4)
    c: Diameter(g0) = 2.6
    c: Tangent(g1,g-6)
    c: Diameter(g1) = 2.6
    c: DistanceY(g0,g-4) = 1.45
    c: DistanceY(g-6,g1) = 1.45
FEATURE [PartDesign::Pad] Pad057
  BaseFeature = -> Pocket063
  Direction = (4.1e-15,-1.7e-15,-1)
  Length = 12
  Length2 = 10
  Placement = pos=(0,0,0) rot=(1,1,1;2.0944rad)
  Profile = -> Sketch116
  ReferenceAxis = -> Sketch116 [N_Axis]
  Refine = true
  Suppressed = false
  Type = 0
FEATURE [Sketcher::SketchObject] Sketch117
  ArcFitTolerance = 1e-06
  AttachmentSupport = -> [Pad057]
  ExternalGeometry = -> [Pad057]
  FullyConstrained = true
  MakeInternals = false
  MapMode = 5
  Placement = pos=(-1.2e-14,5e-15,3.5) rot=(0.707107,0.707107,0;3.14159rad)
  sketch-geometry (1):
    g0: Circle CenterX=8.75 CenterY=10 CenterZ=0 NormalX=0 NormalY=0 NormalZ=1 AngleXU=0 Radius=2.375
  constraints (3):
    c: Diameter(g0) = 4.75
    c: DistanceY(g0,g-4) = 4.05
    c: DistanceX(g0,g-4) = 2.55
FEATURE [PartDesign::Pad] Pad058
  BaseFeature = -> Pad057
  Direction = (4.4e-15,-1.8e-15,-1)
  Length = 4.5
  Length2 = 10
  Placement = pos=(0,0,0) rot=(1,1,1;2.0944rad)
  Profile = -> Sketch117
  ReferenceAxis = -> Sketch117 [N_Axis]
  Refine = true
  Suppressed = false
  Type = 0
FEATURE [Sketcher::SketchObject] Sketch118
  ArcFitTolerance = 1e-06
  AttachmentSupport = -> [Pad058]
  ExternalGeometry = -> [Pad058]
  FullyConstrained = true
  MakeInternals = false
  MapMode = 5
  Placement = pos=(4.4e-15,-1.7e-15,-1) rot=(0.707107,0.707107,0;3.14159rad)
  sketch-geometry (1):
    g0: Circle CenterX=8.75 CenterY=10 CenterZ=0 NormalX=0 NormalY=0 NormalZ=1 AngleXU=0 Radius=0.75
  constraints (2):
    c: Coincident(g0,g-3)
    c: Diameter(g0) = 1.5
FEATURE [PartDesign::Pocket] Pocket064
  BaseFeature = -> Pad058
  Direction = (-4.8e-15,1.8e-15,1)
  Length = 4.5
  Length2 = 5
  Placement = pos=(0,0,0) rot=(1,1,1;2.0944rad)
  Profile = -> Sketch118
  ReferenceAxis = -> Sketch118 [N_Axis]
  Refine = true
  Suppressed = false
  Type = 0
FEATURE [Sketcher::SketchObject] Sketch119
  ArcFitTolerance = 1e-06
  AttachmentSupport = -> [Pocket064]
  ExternalGeometry = -> [Pocket064]
  FullyConstrained = true
  MakeInternals = false
  MapMode = 5
  Placement = pos=(0,0,0) rot=(0.707107,0.707107,0;3.14159rad)
  sketch-geometry (4):
    g0: LineSegment StartX=4.75 StartY=15.5 StartZ=0 EndX=1.5 EndY=15.5 EndZ=0
    g1: LineSegment StartX=1.5 StartY=15.5 StartZ=0 EndX=1.5 EndY=4.5 EndZ=0
    g2: LineSegment StartX=1.5 StartY=4.5 StartZ=0 EndX=4.75 EndY=4.5 EndZ=0
    g3: LineSegment StartX=4.75 StartY=4.5 StartZ=0 EndX=4.75 EndY=15.5 EndZ=0
  constraints (10):
    c: Coincident(g0,g1)
    c: Coincident(g1,g2)
    c: Coincident(g2,g3)
    c: Coincident(g3,g0)
    c: Horizontal(g0)
    c: Horizontal(g2)
    c: Vertical(g1)
    c: Vertical(g3)
    c: Coincident(g0,g-3)
    c: Coincident(g1,g-4)
FEATURE [PartDesign::Pocket] Pocket065
  BaseFeature = -> Pocket064
  Direction = (0,0,1)
  Length = 5
  Length2 = 5
  Placement = pos=(0,0,0) rot=(1,1,1;2.0944rad)
  Profile = -> Sketch119
  ReferenceAxis = -> Sketch119 [N_Axis]
  Refine = true
  Suppressed = false
  Type = 0
FEATURE [Sketcher::SketchObject] Sketch120
  ArcFitTolerance = 1e-06
  AttachmentSupport = -> [Pocket065]
  ExternalGeometry = -> [Pocket065]
  FullyConstrained = true
  MakeInternals = false
  MapMode = 5
  Placement = pos=(0,0,0) rot=(0.57735,0.57735,-0.57735;4.18879rad)
  sketch-geometry (4):
    g0: ArcOfCircle CenterX=3.1 CenterY=-1.5 CenterZ=0 NormalX=0 NormalY=0 NormalZ=1 AngleXU=0 Radius=1 StartAngle=3.14159 EndAngle=6.28319
    g1: LineSegment StartX=4.1 StartY=-1.5 StartZ=0 EndX=4.1 EndY=2.31e-14 EndZ=0
    g2: LineSegment StartX=2.1 StartY=-1.5 StartZ=0 EndX=2.1 EndY=1.18e-14 EndZ=0
    g3: LineSegment StartX=2.1 StartY=1.18e-14 StartZ=0 EndX=4.1 EndY=2.31e-14 EndZ=0
  constraints (13):
    c: Coincident(g1,g0)
    c: PointOnObject(g1,g-3)
    c: Vertical(g1)
    c: Coincident(g2,g0)
    c: PointOnObject(g2,g-3)
    c: Vertical(g2)
    c: Coincident(g3,g2)
    c: Coincident(g3,g1)
    c: Diameter(g0) = 2
    c: DistanceX(g-1,g0) = 3.1
    c: DistanceY(g0,g1) = 1.5
    c: DistanceY(g1,g1) = 1.5
    c: DistanceY(g2,g2) = 1.5
FEATURE [Sketcher::SketchObject] Sketch121
  ArcFitTolerance = 1e-06
  AttachmentSupport = -> [Pocket065]
  ExternalGeometry = -> [Pocket065]
  FullyConstrained = true
  MakeInternals = false
  MapMode = 5
  Placement = pos=(0,0,0) rot=(0.707107,0.707107,0;3.14159rad)
  sketch-geometry (8):
    g0: LineSegment StartX=4.75 StartY=1.5 StartZ=0 EndX=4.75 EndY=0 EndZ=0
    g1: LineSegment StartX=4.75 StartY=0 StartZ=0 EndX=6.65 EndY=0 EndZ=0
    g2: LineSegment StartX=6.65 StartY=0 StartZ=0 EndX=6.65 EndY=1.5 EndZ=0
    g3: LineSegment StartX=6.65 StartY=1.5 StartZ=0 EndX=4.75 EndY=1.5 EndZ=0
    g4: LineSegment StartX=4.75 StartY=20 StartZ=0 EndX=4.75 EndY=18.5 EndZ=0
    g5: LineSegment StartX=4.75 StartY=18.5 StartZ=0 EndX=6.65 EndY=18.5 EndZ=0
    g6: LineSegment StartX=6.65 StartY=18.5 StartZ=0 EndX=6.65 EndY=20 EndZ=0
    g7: LineSegment StartX=6.65 StartY=20 StartZ=0 EndX=4.75 EndY=20 EndZ=0
  constraints (22):
    c: Coincident(g0,g1)
    c: Coincident(g1,g2)
    c: Coincident(g2,g3)
    c: Coincident(g3,g0)
    c: Vertical(g0)
    c: Vertical(g2)
    c: Horizontal(g1)
    c: Horizontal(g3)
    c: Coincident(g0,g-5)
    c: PointOnObject(g1,g-6)
    c: Coincident(g4,g5)
    c: Coincident(g5,g6)
    c: Coincident(g6,g7)
    c: Coincident(g7,g4)
    c: Vertical(g4)
    c: Vertical(g6)
    c: Horizontal(g5)
    c: Horizontal(g7)
    c: Coincident(g4,g-3)
    c: PointOnObject(g5,g-4)
    c: DistanceX(g7,g7) = 1.9
    c: DistanceX(g1,g1) = 1.9
FEATURE [PartDesign::Pad] Pad059
  BaseFeature = -> Pocket065
  Direction = (0,0,-1)
  Length = 8.2
  Length2 = 10
  Placement = pos=(0,0,0) rot=(1,1,1;2.0944rad)
  Profile = -> Sketch121
  ReferenceAxis = -> Sketch121 [N_Axis]
  Refine = true
  Reversed = true
  Suppressed = false
  Type = 0
FEATURE [PartDesign::Pocket] Pocket066
  BaseFeature = -> Pad059
  Direction = (1,0,0)
  Length = 20
  Length2 = 5
  Placement = pos=(0,0,0) rot=(1,1,1;2.0944rad)
  Profile = -> Sketch120
  ReferenceAxis = -> Sketch120 [N_Axis]
  Refine = true
  Suppressed = false
  Type = 0
FEATURE [PartDesign::Fillet] Fillet031
  Base = -> Pocket066 [Edge161,Edge152,Edge160,Edge26,Edge21,Edge24,Edge27,Edge69,Edge22,Edge20,Edge17,Edge18,Edge16,Edge68,Edge81,Edge70,Edge80,Edge79,Edge78,Edge56,Edge77,Edge76,Edge71,Edge72,Edge73,Edge74,Edge75,Edge58,Edge120,Edge15,Edge50,Edge14,Edge1,Edge5,Edge4,Edge177,Edge59,Edge123,Edge134,Edge6,+1 more]
  BaseFeature = -> Pocket066
  Placement = pos=(0,0,0) rot=(1,1,1;2.0944rad)
  Radius = 0.5
  Refine = true
  SupportTransform = false
  Suppressed = false
  UseAllEdges = false
FEATURE [Sketcher::SketchObject] Sketch307
  ArcFitTolerance = 1e-06
  AttachmentSupport = -> [Fillet031]
  ExternalGeometry = -> [Fillet031]
  FullyConstrained = true
  MakeInternals = false
  MapMode = 5
  Placement = pos=(-2.67e-14,1.17e-14,9.6) rot=(0.707107,0.707107,0;3.14159rad)
  sketch-geometry (8):
    g0: LineSegment StartX=1.5 StartY=4.5 StartZ=0 EndX=1.5 EndY=1.5 EndZ=0
    g1: LineSegment StartX=1.5 StartY=1.5 StartZ=0 EndX=2.5 EndY=1.5 EndZ=0
    g2: LineSegment StartX=2.5 StartY=1.5 StartZ=0 EndX=2.5 EndY=4.5 EndZ=0
    g3: LineSegment StartX=2.5 StartY=4.5 StartZ=0 EndX=1.5 EndY=4.5 EndZ=0
    g4: LineSegment StartX=1.5 StartY=18.5 StartZ=0 EndX=1.5 EndY=15.5 EndZ=0
    g5: LineSegment StartX=1.5 StartY=15.5 StartZ=0 EndX=2.5 EndY=15.5 EndZ=0
    g6: LineSegment StartX=2.5 StartY=15.5 StartZ=0 EndX=2.5 EndY=18.5 EndZ=0
    g7: LineSegment StartX=2.5 StartY=18.5 StartZ=0 EndX=1.5 EndY=18.5 EndZ=0
  constraints (22):
    c: Coincident(g0,g1)
    c: Coincident(g1,g2)
    c: Coincident(g2,g3)
    c: Coincident(g3,g0)
    c: Vertical(g0)
    c: Vertical(g2)
    c: Horizontal(g1)
    c: Horizontal(g3)
    c: Coincident(g0,g-3)
    c: PointOnObject(g1,g-4)
    c: Coincident(g4,g5)
    c: Coincident(g5,g6)
    c: Coincident(g6,g7)
    c: Coincident(g7,g4)
    c: Vertical(g4)
    c: Vertical(g6)
    c: Horizontal(g5)
    c: Horizontal(g7)
    c: Coincident(g4,g-5)
    c: PointOnObject(g5,g-6)
    c: DistanceX(g7,g7) = 1
    c: DistanceX(g3,g3) = 1
FEATURE [PartDesign::Pad] Pad176
  BaseFeature = -> Fillet031
  Direction = (3.8e-15,-1.6e-15,-1)
  Length = 3
  Length2 = 10
  Placement = pos=(0,0,0) rot=(1,1,1;2.0944rad)
  Profile = -> Sketch307
  ReferenceAxis = -> Sketch307 [N_Axis]
  Refine = true
  Suppressed = false
  Type = 0
FEATURE [PartDesign::Body] Body010  label="Chest"
  AllowCompound = false
  Group = -> [Sketch102,Pad053,Sketch104,Pocket055,Sketch105,Pocket056,Sketch106,Pocket057,Sketch107,Pocket058,Sketch108,Pocket059,Sketch109,Pad054,Fillet030,Sketch110,Pad055,Sketch111,Pad056,Sketch112,Pocket060,Sketch113,Pocket061,Sketch114,Pocket062,Sketch115,Pocket063,Sketch116,Pad057,Sketch117,Pad058,Sketch118,Pocket064,Sketch119,Pocket065,Sketch120,Sketch121,Pad059,Pocket066,Fillet031,Sketch307,Pad176,+14 more]
  Origin = -> Origin012
  Placement = pos=(48.2,-5,3.2) rot=(0,0,1;3.14159rad)
  Tip = -> Pocket174
COMPONENT P3 — recipe-attached ("Canopy", modeled in this document).
Construction recipe (the document's own serialized feature program — sketch geometry with constraints, then the solid features built on it; lengths are millimeters unless a unit is written):

FEATURE [Sketcher::SketchObject] Sketch122
  ArcFitTolerance = 1e-06
  AttachmentSupport = -> [XY_Plane013]
  FullyConstrained = true
  MakeInternals = false
  MapMode = 5
  sketch-geometry (4):
    g0: ArcOfCircle CenterX=-7.6e-15 CenterY=-39.3225 CenterZ=0 NormalX=0 NormalY=0 NormalZ=1 AngleXU=0 Radius=41.3225 StartAngle=1.2584 EndAngle=1.88319
    g1: LineSegment StartX=-12.7 StartY=0 StartZ=0 EndX=-12.7 EndY=2 EndZ=0
    g2: LineSegment StartX=12.7 StartY=0 StartZ=0 EndX=12.7 EndY=2 EndZ=0
    g3: ArcOfCircle CenterX=3e-15 CenterY=-41.3225 CenterZ=0 NormalX=0 NormalY=0 NormalZ=1 AngleXU=0 Radius=45.1456 StartAngle=1.28564 EndAngle=1.85596
  constraints (14):
    c: PointOnObject(g0,g-1)
    c: PointOnObject(g0,g-1)
    c: DistanceX(g0,g-1) = 12.7
    c: DistanceX(g-1,g0) = 12.7
    c: Distance(g-1,g0) = 2
    c: Coincident(g1,g0)
    c: Vertical(g1)
    c: Coincident(g2,g0)
    c: Vertical(g2)
    c: Coincident(g3,g1)
    c: Coincident(g3,g2)
    c: DistanceY(g1,g1) = 2
    c: DistanceY(g2,g2) = 2
    c: DistanceY(g3,g0) = 2
FEATURE [PartDesign::Pad] Pad060
  Direction = (0,0,1)
  Length = 20.3
  Length2 = 10
  Profile = -> Sketch122
  ReferenceAxis = -> Sketch122 [N_Axis]
  Refine = true
  Suppressed = false
  Type = 0
FEATURE [Sketcher::SketchObject] Sketch123
  ArcFitTolerance = 1e-06
  AttachmentSupport = -> [Pad060]
  ExternalGeometry = -> [Pad060]
  FullyConstrained = false
  MakeInternals = false
  MapMode = 5
  Placement = pos=(-12.7,0,0) rot=(0.57735,-0.57735,-0.57735;2.0944rad)
  sketch-geometry (8):
    g0: LineSegment StartX=0 StartY=4 StartZ=0 EndX=15 EndY=4 EndZ=0
    g1: LineSegment StartX=2.2 StartY=10.8 StartZ=0 EndX=2.2 EndY=7.3 EndZ=0
    g2: LineSegment StartX=-2 StartY=4 StartZ=0 EndX=-2 EndY=13 EndZ=0
    g3: LineSegment StartX=0 StartY=4 StartZ=0 EndX=-2 EndY=4 EndZ=0
    g4: LineSegment StartX=-2 StartY=13 StartZ=0 EndX=0 EndY=13 EndZ=0
    g5: ArcOfCircle CenterX=-2e-16 CenterY=10.8 CenterZ=0 NormalX=0 NormalY=0 NormalZ=1 AngleXU=0 Radius=2.2 StartAngle=0 EndAngle=1.5708
    g6: LineSegment StartX=2.2 StartY=7.3 StartZ=0 EndX=15.2739 EndY=7.3 EndZ=0
    g7: ArcOfCircle CenterX=17.0037 CenterY=5.49507 CenterZ=0 NormalX=0 NormalY=0 NormalZ=1 AngleXU=0 Radius=2.5 StartAngle=3.78263 EndAngle=8.61813
  constraints (25):
    c: PointOnObject(g0,g-2)
    c: DistanceY(g-1,g0) = 4
    c: Horizontal(g0)
    c: DistanceX(g0,g0) = 15
    c: Vertical(g1)
    c: DistanceX(g0,g1) = 2.2
    c: Vertical(g2)
    c: DistanceY(g2,g2) = 9
    c: DistanceY(g0,g2) = 0
    c: Coincident(g3,g0)
    c: Coincident(g3,g2)
    c: Coincident(g4,g2)
    c: PointOnObject(g4,g-2)
    c: Horizontal(g4)
    c: PointOnObject(g2,g-3)
    c: Coincident(g5,g4)
    c: Coincident(g5,g1)
    c: Radius(g5) = 2.2
    c: DistanceY(g5,g1) = 0
    c: Coincident(g6,g1)
    c: Horizontal(g6)
    c: DistanceY(g0,g1) = 3.3
    c: Coincident(g7,g6)
    c: Coincident(g7,g0)
    c: Diameter(g7) = 5
FEATURE [PartDesign::Pad] Pad061
  BaseFeature = -> Pad060
  Direction = (-1,0,0)
  Length = 25.4
  Length2 = 10
  Profile = -> Sketch123
  ReferenceAxis = -> Sketch123 [N_Axis]
  Refine = true
  Reversed = true
  Suppressed = false
  Type = 0
FEATURE [Sketcher::SketchObject] Sketch124
  ArcFitTolerance = 1e-06
  AttachmentSupport = -> [Pad061]
  ExternalGeometry = -> [Pad061]
  FullyConstrained = true
  MakeInternals = false
  MapMode = 5
  Placement = pos=(0,1.755e-13,4) rot=(1,0,0;3.14159rad)
  sketch-geometry (12):
    g0: ArcOfCircle CenterX=0 CenterY=39.3225 CenterZ=0 NormalX=0 NormalY=0 NormalZ=1 AngleXU=0 Radius=41.3225 StartAngle=4.39999 EndAngle=4.42469
    g1: LineSegment StartX=-11.725 StartY=19.6983 StartZ=0 EndX=-11.725 EndY=-0.301651 EndZ=0
    g2: LineSegment StartX=-12.7 StartY=0 StartZ=0 EndX=-12.7 EndY=19.6983 EndZ=0
    g3: LineSegment StartX=-11.725 StartY=19.6983 StartZ=0 EndX=-12.7 EndY=19.6983 EndZ=0
    g4: ArcOfCircle CenterX=0 CenterY=39.3225 CenterZ=0 NormalX=0 NormalY=0 NormalZ=1 AngleXU=0 Radius=41.3225 StartAngle=5.00009 EndAngle=5.02478
    g5: LineSegment StartX=11.725 StartY=-0.301651 StartZ=0 EndX=11.725 EndY=19.6983 EndZ=0
    g6: LineSegment StartX=12.7 StartY=0 StartZ=0 EndX=12.7 EndY=19.6983 EndZ=0
    g7: LineSegment StartX=12.7 StartY=19.6983 StartZ=0 EndX=11.725 EndY=19.6983 EndZ=0
    g8: ArcOfCircle CenterX=8.4e-15 CenterY=39.3225 CenterZ=0 NormalX=0 NormalY=0 NormalZ=1 AngleXU=0 Radius=41.3225 StartAngle=4.46734 EndAngle=4.95744
    g9: LineSegment StartX=-10.025 StartY=-0.765508 StartZ=0 EndX=-10.025 EndY=20.2345 EndZ=0
    g10: LineSegment StartX=10.025 StartY=-0.765508 StartZ=0 EndX=10.025 EndY=20.2345 EndZ=0
    g11: LineSegment StartX=-10.025 StartY=20.2345 StartZ=0 EndX=10.025 EndY=20.2345 EndZ=0
  constraints (36):
    c: Coincident(g0,g-3)
    c: PointOnObject(g0,g-3)
    c: DistanceX(g0,g0) = 0.975
    c: PointOnObject(g0,g-2)
    c: Coincident(g1,g0)
    c: DistanceY(g1,g1) = 20
    c: Coincident(g2,g0)
    c: Vertical(g2)
    c: Coincident(g3,g1)
    c: Coincident(g3,g2)
    c: Horizontal(g3)
    c: Coincident(g4,g-3)
    c: PointOnObject(g4,g-3)
    c: DistanceX(g4,g4) = 0.975
    c: PointOnObject(g4,g-2)
    c: Coincident(g5,g4)
    c: Vertical(g5)
    c: DistanceY(g5,g5) = 20
    c: Coincident(g6,g4)
    c: Vertical(g6)
    c: Coincident(g7,g6)
    c: Coincident(g7,g5)
    c: Horizontal(g7)
    c: Tangent(g8,g-3) = -1.5708
    c: PointOnObject(g8,g-3)
    c: Coincident(g9,g8)
    c: Vertical(g9)
    c: DistanceY(g9,g9) = 21
    c: Coincident(g10,g8)
    c: Vertical(g10)
    c: DistanceY(g10,g10) = 21
    c: Coincident(g11,g9)
    c: Coincident(g11,g10)
    c: DistanceX(g8,g4) = 1.7
    c: DistanceX(g0,g8) = 1.7
    c: Vertical(g1)
FEATURE [PartDesign::Pocket] Pocket067
  BaseFeature = -> Pad061
  Direction = (0,4.39e-14,1)
  Length = 9
  Length2 = 5
  Profile = -> Sketch124
  ReferenceAxis = -> Sketch124 [N_Axis]
  Refine = true
  Suppressed = false
  Type = 0
FEATURE [Sketcher::SketchObject] Sketch125
  ArcFitTolerance = 1e-06
  AttachmentSupport = -> [Pocket067]
  ExternalGeometry = -> [Pocket067]
  FullyConstrained = true
  MakeInternals = false
  MapMode = 5
  Placement = pos=(0,1.754e-13,4) rot=(0,0,1;0rad)
  sketch-geometry (12):
    g0: LineSegment StartX=11.725 StartY=-15 StartZ=0 EndX=11.725 EndY=-19.0074 EndZ=0
    g1: LineSegment StartX=11.725 StartY=-19.0074 StartZ=0 EndX=12.7 EndY=-19.0074 EndZ=0
    g2: LineSegment StartX=12.7 StartY=-19.0074 StartZ=0 EndX=12.7 EndY=-15 EndZ=0
    g3: LineSegment StartX=12.7 StartY=-15 StartZ=0 EndX=11.725 EndY=-15 EndZ=0
    g4: LineSegment StartX=10.025 StartY=-15 StartZ=0 EndX=-10.025 EndY=-15 EndZ=0
    g5: LineSegment StartX=-10.025 StartY=-15 StartZ=0 EndX=-10.025 EndY=-19.0074 EndZ=0
    g6: LineSegment StartX=-10.025 StartY=-19.0074 StartZ=0 EndX=10.025 EndY=-19.0074 EndZ=0
    g7: LineSegment StartX=10.025 StartY=-19.0074 StartZ=0 EndX=10.025 EndY=-15 EndZ=0
    g8: LineSegment StartX=-12.7 StartY=-19.0074 StartZ=0 EndX=-11.725 EndY=-19.0074 EndZ=0
    g9: LineSegment StartX=-11.725 StartY=-19.0074 StartZ=0 EndX=-11.725 EndY=-15 EndZ=0
    g10: LineSegment StartX=-11.725 StartY=-15 StartZ=0 EndX=-12.7 EndY=-15 EndZ=0
    g11: LineSegment StartX=-12.7 StartY=-15 StartZ=0 EndX=-12.7 EndY=-19.0074 EndZ=0
  constraints (30):
    c: Coincident(g0,g1)
    c: Coincident(g1,g2)
    c: Coincident(g2,g3)
    c: Coincident(g3,g0)
    c: Vertical(g0)
    c: Vertical(g2)
    c: Horizontal(g1)
    c: Horizontal(g3)
    c: Coincident(g0,g-5)
    c: Coincident(g1,g-6)
    c: Coincident(g4,g5)
    c: Coincident(g5,g6)
    c: Coincident(g6,g7)
    c: Coincident(g7,g4)
    c: Horizontal(g4)
    c: Horizontal(g6)
    c: Vertical(g5)
    c: Vertical(g7)
    c: Coincident(g4,g-3)
    c: Coincident(g5,g-4)
    c: Coincident(g8,g9)
    c: Coincident(g9,g10)
    c: Coincident(g10,g11)
    c: Coincident(g11,g8)
    c: Horizontal(g8)
    c: Horizontal(g10)
    c: Vertical(g9)
    c: Vertical(g11)
    c: Coincident(g8,g-8)
    c: Coincident(g9,g-7)
FEATURE [PartDesign::Pocket] Pocket068
  BaseFeature = -> Pocket067
  Direction = (0,-4.39e-14,-1)
  Length = 1.5
  Length2 = 5
  Profile = -> Sketch125
  ReferenceAxis = -> Sketch125 [N_Axis]
  Refine = true
  Suppressed = false
  Type = 0
FEATURE [Sketcher::SketchObject] Sketch126
  ArcFitTolerance = 1e-06
  AttachmentSupport = -> [Pocket068]
  ExternalGeometry = -> [Pocket068]
  FullyConstrained = true
  MakeInternals = false
  MapMode = 5
  Placement = pos=(10.025,0,0) rot=(0.57735,-0.57735,-0.57735;2.0944rad)
  sketch-geometry (1):
    g0: Circle CenterX=17.0037 CenterY=5.49507 CenterZ=0 NormalX=0 NormalY=0 NormalZ=1 AngleXU=0 Radius=1
  constraints (2):
    c: Coincident(g0,g-3)
    c: Diameter(g0) = 2
FEATURE [PartDesign::Pad] Pad062
  BaseFeature = -> Pocket068
  Direction = (-1,0,0)
  Length = 1.6
  Length2 = 10
  Profile = -> Sketch126
  ReferenceAxis = -> Sketch126 [N_Axis]
  Refine = true
  Suppressed = false
  Type = 0
FEATURE [Sketcher::SketchObject] Sketch127
  ArcFitTolerance = 1e-06
  AttachmentSupport = -> [Pad062]
  ExternalGeometry = -> [Pad062]
  FullyConstrained = true
  MakeInternals = false
  MapMode = 5
  Placement = pos=(-10.025,0,0) rot=(0.57735,0.57735,0.57735;2.0944rad)
  sketch-geometry (1):
    g0: Circle CenterX=-17.0037 CenterY=5.49507 CenterZ=0 NormalX=0 NormalY=0 NormalZ=1 AngleXU=0 Radius=1
  constraints (2):
    c: Coincident(g0,g-3)
    c: Diameter(g0) = 2
FEATURE [PartDesign::Pad] Pad063
  BaseFeature = -> Pad062
  Direction = (1,0,0)
  Length = 1.6
  Length2 = 10
  Profile = -> Sketch127
  ReferenceAxis = -> Sketch127 [N_Axis]
  Refine = true
  Suppressed = false
  Type = 0
FEATURE [Sketcher::SketchObject] Sketch128
  ArcFitTolerance = 1e-06
  AttachmentSupport = -> [Pad063]
  ExternalGeometry = -> [Pad063]
  FullyConstrained = true
  MakeInternals = false
  MapMode = 5
  Placement = pos=(-8.425,0,0) rot=(0.57735,0.57735,0.57735;2.0944rad)
  sketch-geometry (1):
    g0: Circle CenterX=-17.0037 CenterY=5.49507 CenterZ=0 NormalX=0 NormalY=0 NormalZ=1 AngleXU=0 Radius=1.55
  constraints (2):
    c: Coincident(g0,g-3)
    c: Diameter(g0) = 3.1
FEATURE [PartDesign::Pad] Pad064
  BaseFeature = -> Pad063
  Direction = (1,0,0)
  Length = 1.2
  Length2 = 10
  Profile = -> Sketch128
  ReferenceAxis = -> Sketch128 [N_Axis]
  Refine = true
  Suppressed = false
  Type = 0
FEATURE [Sketcher::SketchObject] Sketch129
  ArcFitTolerance = 1e-06
  AttachmentSupport = -> [Pad064]
  ExternalGeometry = -> [Pad064]
  FullyConstrained = true
  MakeInternals = false
  MapMode = 5
  Placement = pos=(8.425,0,0) rot=(0.57735,-0.57735,-0.57735;2.0944rad)
  sketch-geometry (1):
    g0: Circle CenterX=17.0037 CenterY=5.49507 CenterZ=0 NormalX=0 NormalY=0 NormalZ=1 AngleXU=0 Radius=1.55
  constraints (2):
    c: Coincident(g0,g-3)
    c: Diameter(g0) = 3.1
FEATURE [PartDesign::Pad] Pad065
  BaseFeature = -> Pad064
  Direction = (-1,0,0)
  Length = 1.2
  Length2 = 10
  Profile = -> Sketch129
  ReferenceAxis = -> Sketch129 [N_Axis]
  Refine = true
  Suppressed = false
  Type = 0
FEATURE [PartDesign::Body] Body011  label="Canopy"
  AllowCompound = false
  Group = -> [Sketch122,Pad060,Sketch123,Pad061,Sketch124,Pocket067,Sketch125,Pocket068,Sketch126,Pad062,Sketch127,Pad063,Sketch128,Pad064,Sketch129,Pad065]
  Origin = -> Origin013
  Placement = pos=(38.2,-2.6,21.7) rot=(1,0,0;1.5708rad)
  Tip = -> Pad065
COMPONENT P4 — recipe-attached ("Right_Outer_Leg", modeled in this document).
Construction recipe (the document's own serialized feature program — sketch geometry with constraints, then the solid features built on it; lengths are millimeters unless a unit is written):

FEATURE [Sketcher::SketchObject] Sketch130
  ArcFitTolerance = 1e-06
  AttachmentSupport = -> [XY_Plane014]
  FullyConstrained = true
  MakeInternals = false
  MapMode = 5
  sketch-geometry (4):
    g0: ArcOfCircle CenterX=0 CenterY=0 CenterZ=0 NormalX=0 NormalY=0 NormalZ=1 AngleXU=0 Radius=5.55 StartAngle=1.5708 EndAngle=4.71239
    g1: ArcOfCircle CenterX=42.05 CenterY=4e-16 CenterZ=0 NormalX=0 NormalY=0 NormalZ=1 AngleXU=0 Radius=5.55 StartAngle=4.71239 EndAngle=7.85398
    g2: LineSegment StartX=-3e-15 StartY=5.55 StartZ=0 EndX=42.05 EndY=5.55 EndZ=0
    g3: LineSegment StartX=-1e-15 StartY=-5.55 StartZ=0 EndX=42.05 EndY=-5.55 EndZ=0
  constraints (9):
    c: Tangent(g0,g2) = 1.5708
    c: Tangent(g0,g3) = -1.5708
    c: Tangent(g1,g2) = 1.5708
    c: Tangent(g1,g3) = -1.5708
    c: Equal(g0,g1)
    c: Horizontal(g3)
    c: Coincident(g0,g-1)
    c: DistanceX(g0,g1) = 42.05
    c: Diameter(g0) = 11.1
FEATURE [PartDesign::Pad] Pad066
  Direction = (0,0,1)
  Length = 1.6
  Length2 = 10
  Profile = -> Sketch130
  ReferenceAxis = -> Sketch130 [N_Axis]
  Refine = true
  Suppressed = false
  Type = 0
FEATURE [Sketcher::SketchObject] Sketch131
  ArcFitTolerance = 1e-06
  AttachmentSupport = -> [Pad066]
  ExternalGeometry = -> [Pad066]
  FullyConstrained = true
  MakeInternals = false
  MapMode = 5
  Placement = pos=(0,0,1.6) rot=(0,0,1;0rad)
  sketch-geometry (4):
    g0: ArcOfCircle CenterX=0 CenterY=0 CenterZ=0 NormalX=0 NormalY=0 NormalZ=1 AngleXU=0 Radius=3.5 StartAngle=1.5708 EndAngle=4.71239
    g1: ArcOfCircle CenterX=42.05 CenterY=4e-16 CenterZ=0 NormalX=0 NormalY=0 NormalZ=1 AngleXU=0 Radius=3.5 StartAngle=4.71239 EndAngle=7.85398
    g2: LineSegment StartX=-6e-16 StartY=3.5 StartZ=0 EndX=42.05 EndY=3.5 EndZ=0
    g3: LineSegment StartX=-6e-16 StartY=-3.5 StartZ=0 EndX=42.05 EndY=-3.5 EndZ=0
  constraints (8):
    c: Tangent(g0,g2) = 1.5708
    c: Tangent(g0,g3) = -1.5708
    c: Tangent(g1,g2) = 1.5708
    c: Tangent(g1,g3) = -1.5708
    c: Equal(g0,g1)
    c: Diameter(g0) = 7
    c: Coincident(g0,g-1)
    c: Coincident(g1,g-3)
FEATURE [PartDesign::Pad] Pad067
  BaseFeature = -> Pad066
  Direction = (0,0,1)
  Length = 1
  Length2 = 10
  Profile = -> Sketch131
  ReferenceAxis = -> Sketch131 [N_Axis]
  Refine = true
  Suppressed = false
  Type = 0
FEATURE [Sketcher::SketchObject] Sketch132
  ArcFitTolerance = 1e-06
  AttachmentSupport = -> [Pad067]
  ExternalGeometry = -> [Pad067]
  FullyConstrained = true
  MakeInternals = false
  MapMode = 5
  Placement = pos=(0,0,1.6) rot=(0,0,1;0rad)
  sketch-geometry (14):
    g0: Circle CenterX=42.05 CenterY=0 CenterZ=0 NormalX=0 NormalY=0 NormalZ=1 AngleXU=0 Radius=5.55
    g1: Circle CenterX=0 CenterY=0 CenterZ=0 NormalX=0 NormalY=0 NormalZ=1 AngleXU=0 Radius=5.55
    g2: ArcOfCircle CenterX=13.725 CenterY=3.5 CenterZ=0 NormalX=0 NormalY=0 NormalZ=1 AngleXU=0 Radius=1.85 StartAngle=1e-16 EndAngle=3.14159
    g3: ArcOfCircle CenterX=13.725 CenterY=-3.5 CenterZ=0 NormalX=0 NormalY=0 NormalZ=1 AngleXU=0 Radius=1.85 StartAngle=3.14159 EndAngle=6.28319
    g4: LineSegment StartX=15.575 StartY=3.5 StartZ=0 EndX=15.575 EndY=-3.5 EndZ=0
    g5: LineSegment StartX=11.875 StartY=3.5 StartZ=0 EndX=11.875 EndY=-3.5 EndZ=0
    g6: ArcOfCircle CenterX=21.025 CenterY=3.5 CenterZ=0 NormalX=0 NormalY=0 NormalZ=1 AngleXU=0 Radius=1.85 StartAngle=1e-16 EndAngle=3.14159
    g7: ArcOfCircle CenterX=21.025 CenterY=-3.5 CenterZ=0 NormalX=0 NormalY=0 NormalZ=1 AngleXU=0 Radius=1.85 StartAngle=3.14159 EndAngle=6.28319
    g8: LineSegment StartX=22.875 StartY=3.5 StartZ=0 EndX=22.875 EndY=-3.5 EndZ=0
    g9: LineSegment StartX=19.175 StartY=3.5 StartZ=0 EndX=19.175 EndY=-3.5 EndZ=0
    g10: ArcOfCircle CenterX=28.325 CenterY=3.5 CenterZ=0 NormalX=0 NormalY=0 NormalZ=1 AngleXU=0 Radius=1.85 StartAngle=1e-16 EndAngle=3.14159
    g11: ArcOfCircle CenterX=28.325 CenterY=-3.5 CenterZ=0 NormalX=0 NormalY=0 NormalZ=1 AngleXU=0 Radius=1.85 StartAngle=3.14159 EndAngle=6.28319
    g12: LineSegment StartX=30.175 StartY=3.5 StartZ=0 EndX=30.175 EndY=-3.5 EndZ=0
    g13: LineSegment StartX=26.475 StartY=3.5 StartZ=0 EndX=26.475 EndY=-3.5 EndZ=0
  constraints (33):
    c: Coincident(g0,g-3)
    c: PointOnObject(g-3,g0)
    c: Coincident(g1,g-1)
    c: Tangent(g2,g4) = 1.5708
    c: Tangent(g2,g5) = -1.5708
    c: Tangent(g3,g4) = 1.5708
    c: Tangent(g3,g5) = -1.5708
    c: Equal(g2,g3)
    c: Vertical(g5)
    c: PointOnObject(g2,g-5)
    c: PointOnObject(g3,g-4)
    c: Tangent(g6,g8) = 1.5708
    c: Tangent(g6,g9) = -1.5708
    c: Tangent(g7,g8) = 1.5708
    c: Tangent(g7,g9) = -1.5708
    c: Equal(g6,g7)
    c: Tangent(g10,g12) = 1.5708
    c: Tangent(g10,g13) = -1.5708
    c: Tangent(g11,g12) = 1.5708
    c: Tangent(g11,g13) = -1.5708
    c: Equal(g10,g11)
    c: Vertical(g13)
    c: PointOnObject(g10,g-5)
    c: PointOnObject(g11,g-4)
    c: Vertical(g8)
    c: PointOnObject(g7,g-4)
    c: Diameter(g1) = 11.1
    c: Diameter(g2) = 3.7
    c: Diameter(g6) = 3.7
    c: Diameter(g10) = 3.7
    c: DistanceX(g3,g7) = 3.6
    c: DistanceX(g7,g11) = 3.6
    c: Symmetric(g-5,g-5,g6)
FEATURE [PartDesign::Pad] Pad068
  BaseFeature = -> Pad067
  Direction = (0,0,1)
  Length = 0.5
  Length2 = 10
  Profile = -> Sketch132
  ReferenceAxis = -> Sketch132 [N_Axis]
  Refine = true
  Suppressed = false
  Type = 0
FEATURE [Sketcher::SketchObject] Sketch133
  ArcFitTolerance = 1e-06
  AttachmentSupport = -> [Pad068]
  ExternalGeometry = -> [Pad068]
  FullyConstrained = true
  MakeInternals = false
  MapMode = 5
  Placement = pos=(0,0,2.6) rot=(0,0,1;0rad)
  sketch-geometry (2):
    g0: Circle CenterX=0 CenterY=0 CenterZ=0 NormalX=0 NormalY=0 NormalZ=1 AngleXU=0 Radius=4.45
    g1: Circle CenterX=42.05 CenterY=0 CenterZ=0 NormalX=0 NormalY=0 NormalZ=1 AngleXU=0 Radius=4.45
  constraints (4):
    c: Coincident(g0,g-1)
    c: Coincident(g1,g-3)
    c: Diameter(g0) = 8.9
    c: Diameter(g1) = 8.9
FEATURE [PartDesign::Pad] Pad069
  BaseFeature = -> Pad068
  Direction = (0,0,1)
  Length = 1
  Length2 = 10
  Profile = -> Sketch133
  ReferenceAxis = -> Sketch133 [N_Axis]
  Refine = true
  Reversed = true
  Suppressed = false
  Type = 0
FEATURE [Sketcher::SketchObject] Sketch134
  ArcFitTolerance = 1e-06
  AttachmentSupport = -> [Pad069]
  ExternalGeometry = -> [Pad069]
  FullyConstrained = true
  MakeInternals = false
  MapMode = 5
  Placement = pos=(0,0,2.6) rot=(0,0,1;0rad)
  sketch-geometry (2):
    g0: Circle CenterX=42.05 CenterY=0 CenterZ=0 NormalX=0 NormalY=0 NormalZ=1 AngleXU=0 Radius=3.5
    g1: Circle CenterX=0 CenterY=0 CenterZ=0 NormalX=0 NormalY=0 NormalZ=1 AngleXU=0 Radius=3.5
  constraints (4):
    c: Coincident(g0,g-3)
    c: Coincident(g1,g-1)
    c: Diameter(g1) = 7
    c: Diameter(g0) = 7
FEATURE [PartDesign::Pocket] Pocket069
  BaseFeature = -> Pad069
  Direction = (0,0,-1)
  Length = 1
  Length2 = 5
  Profile = -> Sketch134
  ReferenceAxis = -> Sketch134 [N_Axis]
  Refine = true
  Suppressed = false
  Type = 0
FEATURE [Sketcher::SketchObject] Sketch135
  ArcFitTolerance = 1e-06
  AttachmentSupport = -> [Pocket069]
  ExternalGeometry = -> [Pocket069]
  FullyConstrained = true
  MakeInternals = false
  MapMode = 5
  Placement = pos=(0,0,1.6) rot=(0,0,1;0rad)
  sketch-geometry (1):
    g0: Circle CenterX=42.05 CenterY=0 CenterZ=0 NormalX=0 NormalY=0 NormalZ=1 AngleXU=0 Radius=2.5
  constraints (2):
    c: Coincident(g0,g-3)
    c: Diameter(g0) = 5
FEATURE [PartDesign::Pocket] Pocket070
  BaseFeature = -> Pocket069
  Direction = (0,0,-1)
  Length = 2
  Length2 = 5
  Profile = -> Sketch135
  ReferenceAxis = -> Sketch135 [N_Axis]
  Refine = true
  Suppressed = false
  Type = 0
FEATURE [Sketcher::SketchObject] Sketch136
  ArcFitTolerance = 1e-06
  AttachmentSupport = -> [Pocket070]
  FullyConstrained = true
  MakeInternals = false
  MapMode = 5
  Placement = pos=(0,0,1.6) rot=(0,0,1;0rad)
  sketch-geometry (1):
    g0: Circle CenterX=0 CenterY=0 CenterZ=0 NormalX=0 NormalY=0 NormalZ=1 AngleXU=0 Radius=3
  constraints (2):
    c: Coincident(g0,g-1)
    c: Diameter(g0) = 6
FEATURE [PartDesign::Pad] Pad070
  BaseFeature = -> Pocket070
  Direction = (0,0,1)
  Length = 1
  Length2 = 10
  Profile = -> Sketch136
  ReferenceAxis = -> Sketch136 [N_Axis]
  Refine = true
  Suppressed = false
  Type = 0
FEATURE [Sketcher::SketchObject] Sketch137
  ArcFitTolerance = 1e-06
  AttachmentSupport = -> [Pad070]
  FullyConstrained = true
  MakeInternals = false
  MapMode = 5
  Placement = pos=(0,0,2.6) rot=(0,0,1;0rad)
  sketch-geometry (1):
    g0: Circle CenterX=0 CenterY=0 CenterZ=0 NormalX=0 NormalY=0 NormalZ=1 AngleXU=0 Radius=1.95
  constraints (2):
    c: Coincident(g0,g-1)
    c: Diameter(g0) = 3.9
FEATURE [PartDesign::Pad] Pad071
  BaseFeature = -> Pad070
  Direction = (0,0,1)
  Length = 1
  Length2 = 10
  Profile = -> Sketch137
  ReferenceAxis = -> Sketch137 [N_Axis]
  Refine = true
  Suppressed = false
  Type = 0
FEATURE [PartDesign::Fillet] Fillet032
  Base = -> Pad071 [Edge90]
  BaseFeature = -> Pad071
  Radius = 0.5
  Refine = true
  SupportTransform = false
  Suppressed = false
  UseAllEdges = false
FEATURE [Sketcher::SketchObject] Sketch138
  ArcFitTolerance = 1e-06
  AttachmentSupport = -> [Fillet032]
  FullyConstrained = true
  MakeInternals = false
  MapMode = 5
  Placement = pos=(0,0,3.6) rot=(0,0,1;0rad)
  sketch-geometry (8):
    g0: ArcOfCircle CenterX=0 CenterY=1.25 CenterZ=0 NormalX=0 NormalY=0 NormalZ=1 AngleXU=0 Radius=0.375 StartAngle=4e-16 EndAngle=3.14159
    g1: ArcOfCircle CenterX=0 CenterY=-1.25 CenterZ=0 NormalX=0 NormalY=0 NormalZ=1 AngleXU=0 Radius=0.375 StartAngle=3.14159 EndAngle=6.28319
    g2: LineSegment StartX=0.375 StartY=1.25 StartZ=0 EndX=0.375 EndY=-1.25 EndZ=0
    g3: LineSegment StartX=-0.375 StartY=1.25 StartZ=0 EndX=-0.375 EndY=-1.25 EndZ=0
    g4: ArcOfCircle CenterX=-1.25 CenterY=0 CenterZ=0 NormalX=0 NormalY=0 NormalZ=1 AngleXU=0 Radius=0.375 StartAngle=1.5708 EndAngle=4.71239
    g5: ArcOfCircle CenterX=1.25 CenterY=0 CenterZ=0 NormalX=0 NormalY=0 NormalZ=1 AngleXU=0 Radius=0.375 StartAngle=4.71239 EndAngle=7.85398
    g6: LineSegment StartX=-1.25 StartY=0.375 StartZ=0 EndX=1.25 EndY=0.375 EndZ=0
    g7: LineSegment StartX=-1.25 StartY=-0.375 StartZ=0 EndX=1.25 EndY=-0.375 EndZ=0
  constraints (20):
    c: Tangent(g0,g2) = 1.5708
    c: Tangent(g0,g3) = -1.5708
    c: Tangent(g1,g2) = 1.5708
    c: Tangent(g1,g3) = -1.5708
    c: Equal(g0,g1)
    c: Vertical(g3)
    c: PointOnObject(g0,g-2)
    c: Tangent(g4,g6) = 1.5708
    c: Tangent(g4,g7) = -1.5708
    c: Tangent(g5,g6) = 1.5708
    c: Tangent(g5,g7) = -1.5708
    c: Equal(g4,g5)
    c: Horizontal(g7)
    c: Diameter(g0) = 0.75
    c: Diameter(g5) = 0.75
    c: PointOnObject(g5,g-1)
    c: DistanceX(g4,g-1) = 1.25
    c: DistanceX(g-1,g5) = 1.25
    c: DistanceY(g-1,g0) = 1.25
    c: DistanceY(g1,g-1) = 1.25
FEATURE [PartDesign::Pocket] Pocket071
  BaseFeature = -> Fillet032
  Direction = (0,0,-1)
  Length = 0.5
  Length2 = 5
  Profile = -> Sketch138
  ReferenceAxis = -> Sketch138 [N_Axis]
  Refine = true
  Suppressed = false
  Type = 0
FEATURE [Sketcher::SketchObject] Sketch139
  ArcFitTolerance = 1e-06
  AttachmentSupport = -> [Pocket071]
  ExternalGeometry = -> [Pocket071]
  FullyConstrained = true
  MakeInternals = false
  MapMode = 5
  Placement = pos=(0,0,1.6) rot=(0,0,1;0rad)
  sketch-geometry (6):
    g0: ArcOfCircle CenterX=0 CenterY=0 CenterZ=0 NormalX=0 NormalY=0 NormalZ=1 AngleXU=0 Radius=7.05 StartAngle=1.5708 EndAngle=4.71239
    g1: LineSegment StartX=4e-16 StartY=7.05 StartZ=0 EndX=35.05 EndY=7.05 EndZ=0
    g2: LineSegment StartX=-1.3e-15 StartY=-7.05 StartZ=0 EndX=19.175 EndY=-7.05 EndZ=0
    g3: LineSegment StartX=19.175 StartY=-7.05 StartZ=0 EndX=19.175 EndY=0 EndZ=0
    g4: LineSegment StartX=35.05 StartY=7.05 StartZ=0 EndX=35.05 EndY=0 EndZ=0
    g5: LineSegment StartX=35.05 StartY=0 StartZ=0 EndX=19.175 EndY=0 EndZ=0
  constraints (17):
    c: PointOnObject(g0,g-2)
    c: PointOnObject(g0,g-2)
    c: Coincident(g0,g-1)
    c: Diameter(g0) = 14.1
    c: Coincident(g1,g0)
    c: Horizontal(g1)
    c: DistanceX(g1,g-4) = 7
    c: Tangent(g2,g0) = -1.5708
    c: DistanceX(g-6,g2) = 0
    c: Coincident(g3,g2)
    c: PointOnObject(g3,g-1)
    c: Vertical(g3)
    c: PointOnObject(g4,g-1)
    c: Vertical(g4)
    c: Coincident(g5,g4)
    c: Coincident(g5,g3)
    c: Coincident(g4,g1)
FEATURE [PartDesign::Pad] Pad072
  BaseFeature = -> Pocket071
  Direction = (0,0,1)
  Length = 4.05
  Length2 = 10
  Profile = -> Sketch139
  ReferenceAxis = -> Sketch139 [N_Axis]
  Refine = true
  Reversed = true
  Suppressed = false
  Type = 0
FEATURE [Sketcher::SketchObject] Sketch140
  ArcFitTolerance = 1e-06
  AttachmentSupport = -> [Pad072]
  ExternalGeometry = -> [Pad072]
  FullyConstrained = true
  MakeInternals = false
  MapMode = 5
  Placement = pos=(0,0,1.6) rot=(0,0,1;0rad)
  sketch-geometry (8):
    g0: ArcOfCircle CenterX=0 CenterY=1e-16 CenterZ=0 NormalX=0 NormalY=0 NormalZ=1 AngleXU=0 Radius=5.55 StartAngle=1.5708 EndAngle=4.71239
    g1: LineSegment StartX=-1e-15 StartY=-5.55 StartZ=0 EndX=19.175 EndY=-5.55 EndZ=0
    g2: LineSegment StartX=-1.08e-14 StartY=5.55 StartZ=0 EndX=35.05 EndY=5.55 EndZ=0
    g3: ArcOfCircle CenterX=0 CenterY=1e-16 CenterZ=0 NormalX=0 NormalY=0 NormalZ=1 AngleXU=0 Radius=6.05 StartAngle=1.5708 EndAngle=4.71239
    g4: LineSegment StartX=4e-16 StartY=6.05 StartZ=0 EndX=35.05 EndY=6.05 EndZ=0
    g5: LineSegment StartX=35.05 StartY=6.05 StartZ=0 EndX=35.05 EndY=5.55 EndZ=0
    g6: LineSegment StartX=-1.1e-15 StartY=-6.05 StartZ=0 EndX=19.175 EndY=-6.05 EndZ=0
    g7: LineSegment StartX=19.175 StartY=-6.05 StartZ=0 EndX=19.175 EndY=-5.55 EndZ=0
  constraints (21):
    c: Coincident(g0,g-3)
    c: Tangent(g1,g0) = -1.5708
    c: Coincident(g1,g-4)
    c: Coincident(g2,g0)
    c: Coincident(g2,g-5)
    c: Diameter(g-3) = 11.1
    c: PointOnObject(g3,g-2)
    c: PointOnObject(g3,g-2)
    c: Diameter(g3) = 12.1
    c: Coincident(g3,g0)
    c: Coincident(g5,g4)
    c: Coincident(g5,g2)
    c: Vertical(g5)
    c: Tangent(g6,g3) = -1.5708
    c: PointOnObject(g6,g-4)
    c: Horizontal(g6)
    c: Coincident(g7,g6)
    c: Coincident(g7,g1)
    c: Horizontal(g1)
    c: Horizontal(g4)
    c: Coincident(g4,g3)
FEATURE [PartDesign::Pocket] Pocket072
  BaseFeature = -> Pad072
  Direction = (0,0,-1)
  Length = 0.5
  Length2 = 5
  Profile = -> Sketch140
  ReferenceAxis = -> Sketch140 [N_Axis]
  Refine = true
  Suppressed = false
  Type = 0
FEATURE [Sketcher::SketchObject] Sketch141
  ArcFitTolerance = 1e-06
  AttachmentSupport = -> [Pocket072]
  ExternalGeometry = -> [Pocket072]
  FullyConstrained = true
  MakeInternals = false
  MapMode = 5
  Placement = pos=(0,0,-2.45) rot=(1,0,0;3.14159rad)
  sketch-geometry (6):
    g0: LineSegment StartX=19.175 StartY=5.55 StartZ=0 EndX=0 EndY=5.55 EndZ=0
    g1: LineSegment StartX=35.05 StartY=-5.55 StartZ=0 EndX=0 EndY=-5.55 EndZ=0
    g2: ArcOfCircle CenterX=0 CenterY=0 CenterZ=0 NormalX=0 NormalY=0 NormalZ=1 AngleXU=0 Radius=5.55 StartAngle=1.5708 EndAngle=4.71239
    g3: LineSegment StartX=35.05 StartY=-5.55 StartZ=0 EndX=35.05 EndY=0 EndZ=0
    g4: LineSegment StartX=35.05 StartY=0 StartZ=0 EndX=19.175 EndY=0 EndZ=0
    g5: LineSegment StartX=19.175 StartY=0 StartZ=0 EndX=19.175 EndY=5.55 EndZ=0
  constraints (16):
    c: PointOnObject(g0,g-3)
    c: PointOnObject(g0,g-2)
    c: Horizontal(g0)
    c: PointOnObject(g1,g-4)
    c: PointOnObject(g1,g-2)
    c: Horizontal(g1)
    c: Coincident(g2,g0)
    c: Coincident(g2,g1)
    c: DistanceY(g0,g-3) = 1.5
    c: Coincident(g2,g-1)
    c: Coincident(g3,g1)
    c: Coincident(g3,g-4)
    c: Coincident(g4,g3)
    c: Coincident(g4,g-3)
    c: Coincident(g5,g4)
    c: Coincident(g5,g0)
FEATURE [PartDesign::Pocket] Pocket073
  BaseFeature = -> Pocket072
  Direction = (0,0,1)
  Length = 2.45
  Length2 = 5
  Profile = -> Sketch141
  ReferenceAxis = -> Sketch141 [N_Axis]
  Refine = true
  Suppressed = false
  Type = 0
FEATURE [Sketcher::SketchObject] Sketch179
  ArcFitTolerance = 1e-06
  AttachmentSupport = -> [Pocket073]
  ExternalGeometry = -> [Pocket073]
  FullyConstrained = true
  MakeInternals = false
  MapMode = 5
  Placement = pos=(0,0,1.6) rot=(0,0,1;0rad)
  sketch-geometry (38):
    g0: ArcOfCircle CenterX=18.575 CenterY=-7.05 CenterZ=0 NormalX=0 NormalY=0 NormalZ=1 AngleXU=0 Radius=0.6 StartAngle=3.14159 EndAngle=6.28319
    g1: ArcOfCircle CenterX=14.675 CenterY=-7.05 CenterZ=0 NormalX=0 NormalY=0 NormalZ=1 AngleXU=0 Radius=0.6 StartAngle=3.14159 EndAngle=6.28319
    g2: ArcOfCircle CenterX=10.775 CenterY=-7.05 CenterZ=0 NormalX=0 NormalY=0 NormalZ=1 AngleXU=0 Radius=0.6 StartAngle=3.14159 EndAngle=6.28319
    g3: ArcOfCircle CenterX=6.875 CenterY=-7.05 CenterZ=0 NormalX=0 NormalY=0 NormalZ=1 AngleXU=0 Radius=0.6 StartAngle=3.14159 EndAngle=6.28319
    g4: ArcOfCircle CenterX=2.975 CenterY=-7.05 CenterZ=0 NormalX=0 NormalY=0 NormalZ=1 AngleXU=0 Radius=0.6 StartAngle=3.14159 EndAngle=6.28319
    g5: ArcOfCircle CenterX=-7.05 CenterY=0 CenterZ=0 NormalX=0 NormalY=0 NormalZ=1 AngleXU=0 Radius=0.6 StartAngle=1.52823 EndAngle=4.75496
    g6: ArcOfCircle CenterX=-0.922632 CenterY=-6.98937 CenterZ=0 NormalX=0 NormalY=0 NormalZ=1 AngleXU=0 Radius=0.6 StartAngle=2.96778 EndAngle=6.19451
    g7: ArcOfCircle CenterX=-5.30094 CenterY=-4.64785 CenterZ=0 NormalX=0 NormalY=0 NormalZ=1 AngleXU=0 Radius=0.6 StartAngle=2.24808 EndAngle=5.4748
    g8: ArcOfCircle CenterX=-5.30161 CenterY=4.64708 CenterZ=0 NormalX=0 NormalY=0 NormalZ=1 AngleXU=0 Radius=0.6 StartAngle=0.808528 EndAngle=4.03525
    g9: ArcOfCircle CenterX=-0.923647 CenterY=6.98923 CenterZ=0 NormalX=0 NormalY=0 NormalZ=1 AngleXU=0 Radius=0.6 StartAngle=0.0888255 EndAngle=3.31555
    g10: ArcOfCircle CenterX=2.97399 CenterY=7.05 CenterZ=0 NormalX=0 NormalY=0 NormalZ=1 AngleXU=0 Radius=0.6 StartAngle=0 EndAngle=3.14159
    g11: ArcOfCircle CenterX=6.87399 CenterY=7.05 CenterZ=0 NormalX=0 NormalY=0 NormalZ=1 AngleXU=0 Radius=0.6 StartAngle=0 EndAngle=3.14159
    g12: ArcOfCircle CenterX=10.774 CenterY=7.05 CenterZ=0 NormalX=0 NormalY=0 NormalZ=1 AngleXU=0 Radius=0.6 StartAngle=5e-16 EndAngle=3.14159
    g13: ArcOfCircle CenterX=14.674 CenterY=7.05 CenterZ=0 NormalX=0 NormalY=0 NormalZ=1 AngleXU=0 Radius=0.6 StartAngle=0 EndAngle=3.14159
    g14: ArcOfCircle CenterX=18.574 CenterY=7.05 CenterZ=0 NormalX=0 NormalY=0 NormalZ=1 AngleXU=0 Radius=0.6 StartAngle=1.5708 EndAngle=3.14159
    g15: ArcOfCircle CenterX=19.874 CenterY=7.05 CenterZ=0 NormalX=0 NormalY=0 NormalZ=1 AngleXU=0 Radius=0.6 StartAngle=6e-16 EndAngle=1.5708
    g16: LineSegment StartX=19.874 StartY=7.65 StartZ=0 EndX=18.574 EndY=7.65 EndZ=0
    g17: ArcOfCircle CenterX=23.774 CenterY=7.05 CenterZ=0 NormalX=0 NormalY=0 NormalZ=1 AngleXU=0 Radius=0.6 StartAngle=5e-16 EndAngle=3.14159
    g18: ArcOfCircle CenterX=27.674 CenterY=7.05 CenterZ=0 NormalX=0 NormalY=0 NormalZ=1 AngleXU=0 Radius=0.6 StartAngle=1e-16 EndAngle=3.14159
    g19: ArcOfCircle CenterX=31.574 CenterY=7.05 CenterZ=0 NormalX=0 NormalY=0 NormalZ=1 AngleXU=0 Radius=0.6 StartAngle=2e-16 EndAngle=3.14159
    g20: LineSegment StartX=32.174 StartY=7.05 StartZ=0 EndX=30.974 EndY=7.05 EndZ=0
    g21: LineSegment StartX=28.274 StartY=7.05 StartZ=0 EndX=27.074 EndY=7.05 EndZ=0
    g22: LineSegment StartX=24.374 StartY=7.05 StartZ=0 EndX=23.174 EndY=7.05 EndZ=0
    g23: LineSegment StartX=20.474 StartY=7.05 StartZ=0 EndX=17.974 EndY=7.05 EndZ=0
    g24: LineSegment StartX=15.274 StartY=7.05 StartZ=0 EndX=14.074 EndY=7.05 EndZ=0
    g25: LineSegment StartX=11.374 StartY=7.05 StartZ=0 EndX=10.174 EndY=7.05 EndZ=0
    g26: LineSegment StartX=7.47399 StartY=7.05 StartZ=0 EndX=6.27399 EndY=7.05 EndZ=0
    g27: LineSegment StartX=3.57399 StartY=7.05 StartZ=0 EndX=2.37399 EndY=7.05 EndZ=0
    g28: LineSegment StartX=-0.326013 StartY=7.04246 StartZ=0 EndX=-1.51459 EndY=6.88538 EndZ=0
    g29: LineSegment StartX=-4.88728 StartY=5.08105 StartZ=0 EndX=-5.67755 EndY=4.17946 EndZ=0
    g30: LineSegment StartX=-7.02447 StartY=0.599457 StartZ=0 EndX=-7.02447 EndY=-0.599457 EndZ=0
    g31: LineSegment StartX=-5.67694 StartY=-4.18029 StartZ=0 EndX=-4.88654 EndY=-5.08176 EndZ=0
    g32: LineSegment StartX=-0.32499 StartY=-7.04251 StartZ=0 EndX=-1.51359 EndY=-6.8856 EndZ=0
    g33: LineSegment StartX=2.375 StartY=-7.05 StartZ=0 EndX=3.575 EndY=-7.05 EndZ=0
    g34: LineSegment StartX=6.275 StartY=-7.05 StartZ=0 EndX=7.475 EndY=-7.05 EndZ=0
    g35: LineSegment StartX=10.175 StartY=-7.05 StartZ=0 EndX=11.375 EndY=-7.05 EndZ=0
    g36: LineSegment StartX=14.075 StartY=-7.05 StartZ=0 EndX=15.275 EndY=-7.05 EndZ=0
    g37: LineSegment StartX=17.975 StartY=-7.05 StartZ=0 EndX=19.175 EndY=-7.05 EndZ=0
  constraints (132):
    c: Coincident(g0,g-3)
    c: PointOnObject(g0,g-3)
    c: PointOnObject(g1,g-3)
    c: PointOnObject(g1,g-3)
    c: PointOnObject(g2,g-3)
    c: PointOnObject(g2,g-3)
    c: PointOnObject(g3,g-3)
    c: PointOnObject(g3,g-3)
    c: PointOnObject(g4,g-3)
    c: PointOnObject(g4,g-3)
    c: Radius(g4) = 0.6
    c: Radius(g3) = 0.6
    c: Radius(g2) = 0.6
    c: Radius(g1) = 0.6
    c: Radius(g0) = 0.6
    c: DistanceX(g1,g0) = 2.7
    c: PointOnObject(g4,g-3)
    c: PointOnObject(g3,g-3)
    c: PointOnObject(g2,g-3)
    c: PointOnObject(g1,g-3)
    c: PointOnObject(g0,g-3)
    c: DistanceX(g2,g1) = 2.7
    c: DistanceX(g3,g2) = 2.7
    c: DistanceX(g4,g3) = 2.7
    c: PointOnObject(g5,g-4)
    c: PointOnObject(g5,g-4)
    c: PointOnObject(g6,g-4)
    c: PointOnObject(g6,g-4)
    c: PointOnObject(g7,g-4)
    c: PointOnObject(g7,g-4)
    c: Distance(g4,g6) = 2.7
    c: Radius(g6) = 0.6
    c: Radius(g7) = 0.6
    c: Radius(g5) = 0.6
    c: PointOnObject(g5,g-4)
    c: PointOnObject(g5,g-1)
    c: PointOnObject(g6,g-4)
    c: PointOnObject(g7,g-4)
    c: Distance(g6,g7) = 3.825
    c: PointOnObject(g8,g-4)
    c: PointOnObject(g8,g-4)
    c: PointOnObject(g9,g-4)
    c: PointOnObject(g9,g-4)
    c: Radius(g8) = 0.6
    c: Radius(g9) = 0.6
    c: Radius(g10) = 0.6
    c: Radius(g11) = 0.6
    c: Radius(g12) = 0.6
    c: PointOnObject(g9,g-4)
    c: PointOnObject(g8,g-4)
    c: Distance(g5,g8) = 3.825
    c: Distance(g8,g9) = 3.825
    c: DistanceX(g9,g10) = 2.7
    c: DistanceX(g10,g11) = 2.7
    c: DistanceX(g11,g12) = 2.7
    c: Radius(g13) = 0.6
    c: DistanceX(g12,g13) = 2.7
    c: Coincident(g16,g15)
    c: Coincident(g16,g14)
    c: Horizontal(g16)
    c: Radius(g14) = 0.6
    c: Radius(g15) = 0.6
    c: DistanceX(g15,g15) = 0
    c: DistanceX(g14,g14) = 0
    c: DistanceX(g13,g14) = 2.7
    c: PointOnObject(g13,g-5)
    c: PointOnObject(g12,g-5)
    c: PointOnObject(g11,g-5)
    c: PointOnObject(g10,g-5)
    c: PointOnObject(g12,g-5)
    c: PointOnObject(g12,g-5)
    c: PointOnObject(g10,g-5)
    c: PointOnObject(g10,g-5)
    c: PointOnObject(g11,g-5)
    c: PointOnObject(g11,g-5)
    c: PointOnObject(g13,g-5)
    c: PointOnObject(g13,g-5)
    c: PointOnObject(g14,g-5)
    c: PointOnObject(g14,g-5)
    c: PointOnObject(g15,g-5)
    c: DistanceX(g14,g15) = 2.5
    c: PointOnObject(g17,g-5)
    c: PointOnObject(g17,g-5)
    c: PointOnObject(g18,g-5)
    c: PointOnObject(g18,g-5)
    c: PointOnObject(g19,g-5)
    c: PointOnObject(g19,g-5)
    c: Radius(g17) = 0.6
    c: Radius(g18) = 0.6
    c: Radius(g19) = 0.6
    c: DistanceX(g15,g17) = 2.7
    c: DistanceX(g17,g18) = 2.7
    c: DistanceX(g18,g19) = 2.7
    c: PointOnObject(g19,g-5)
    c: PointOnObject(g18,g-5)
    c: PointOnObject(g17,g-5)
    c: Coincident(g20,g19)
    c: Coincident(g20,g19)
    c: Coincident(g21,g18)
    c: Coincident(g21,g18)
    c: Coincident(g22,g17)
    c: Coincident(g22,g17)
    c: Coincident(g23,g15)
    c: Coincident(g23,g14)
    c: Coincident(g24,g13)
    c: Coincident(g24,g13)
    c: Coincident(g25,g12)
    c: Coincident(g25,g12)
    c: Coincident(g26,g11)
    c: Coincident(g26,g11)
    c: Coincident(g27,g10)
    c: Coincident(g27,g10)
    c: Coincident(g28,g9)
    c: Coincident(g28,g9)
    c: Coincident(g29,g8)
    c: Coincident(g29,g8)
    c: Coincident(g30,g5)
    c: Coincident(g30,g5)
    c: Coincident(g31,g7)
    c: Coincident(g31,g7)
    c: Coincident(g32,g6)
    c: Coincident(g32,g6)
    c: Coincident(g33,g4)
    c: Coincident(g33,g4)
    c: Coincident(g34,g3)
    c: Coincident(g34,g3)
    c: Coincident(g35,g2)
    c: Coincident(g35,g2)
    c: Coincident(g36,g1)
    c: Coincident(g36,g1)
    c: Coincident(g37,g0)
    c: Coincident(g37,g0)
FEATURE [PartDesign::Pad] Pad094
  BaseFeature = -> Pocket073
  Direction = (0,0,1)
  Length = 4.05
  Length2 = 10
  Profile = -> Sketch179
  ReferenceAxis = -> Sketch179 [N_Axis]
  Refine = true
  Reversed = true
  Suppressed = false
  Type = 0
FEATURE [Sketcher::SketchObject] Sketch180
  ArcFitTolerance = 1e-06
  AttachmentSupport = -> [Pad094]
  ExternalGeometry = -> [Pad094]
  FullyConstrained = true
  MakeInternals = false
  MapMode = 5
  Placement = pos=(0,0,3e-16) rot=(1,0,0;3.14159rad)
  sketch-geometry (8):
    g0: LineSegment StartX=-3 StartY=2.35 StartZ=0 EndX=-3 EndY=-2.35 EndZ=0
    g1: LineSegment StartX=-3 StartY=-2.35 StartZ=0 EndX=-1.6 EndY=-2.35 EndZ=0
    g2: LineSegment StartX=-1.6 StartY=-2.35 StartZ=0 EndX=-1.6 EndY=2.35 EndZ=0
    g3: LineSegment StartX=-1.6 StartY=2.35 StartZ=0 EndX=-3 EndY=2.35 EndZ=0
    g4: LineSegment StartX=1.6 StartY=2.35 StartZ=0 EndX=1.6 EndY=-2.35 EndZ=0
    g5: LineSegment StartX=1.6 StartY=-2.35 StartZ=0 EndX=3 EndY=-2.35 EndZ=0
    g6: LineSegment StartX=3 StartY=-2.35 StartZ=0 EndX=3 EndY=2.35 EndZ=0
    g7: LineSegment StartX=3 StartY=2.35 StartZ=0 EndX=1.6 EndY=2.35 EndZ=0
  constraints (24):
    c: Coincident(g0,g1)
    c: Coincident(g1,g2)
    c: Coincident(g2,g3)
    c: Coincident(g3,g0)
    c: Vertical(g0)
    c: Vertical(g2)
    c: Horizontal(g1)
    c: Horizontal(g3)
    c: Coincident(g4,g5)
    c: Coincident(g5,g6)
    c: Coincident(g6,g7)
    c: Coincident(g7,g4)
    c: Vertical(g4)
    c: Vertical(g6)
    c: Horizontal(g5)
    c: Horizontal(g7)
    c: DistanceY(g0,g0) = 4.7
    c: DistanceY(g4,g4) = 4.7
    c: DistanceX(g3,g3) = 1.4
    c: DistanceX(g7,g7) = 1.4
    c: DistanceY(g4,g-3) = 3.2
    c: DistanceY(g2,g-3) = 3.2
    c: DistanceX(g1,g4) = 3.2
    c: DistanceX(g2,g-1) = 1.6
FEATURE [PartDesign::Pad] Pad095
  BaseFeature = -> Pad094
  Direction = (0,0,-1)
  Length = 4.9
  Length2 = 10
  Profile = -> Sketch180
  ReferenceAxis = -> Sketch180 [N_Axis]
  Refine = true
  Suppressed = false
  Type = 0
FEATURE [Sketcher::SketchObject] Sketch181
  ArcFitTolerance = 1e-06
  AttachmentSupport = -> [Pad095]
  ExternalGeometry = -> [Pad095]
  FullyConstrained = true
  MakeInternals = false
  MapMode = 5
  Placement = pos=(0,0,-4.9) rot=(1,0,0;3.14159rad)
  sketch-geometry (8):
    g0: LineSegment StartX=-3 StartY=1.45 StartZ=0 EndX=-3 EndY=-1.45 EndZ=0
    g1: LineSegment StartX=-3 StartY=-1.45 StartZ=0 EndX=-1.6 EndY=-1.45 EndZ=0
    g2: LineSegment StartX=-1.6 StartY=-1.45 StartZ=0 EndX=-1.6 EndY=1.45 EndZ=0
    g3: LineSegment StartX=-1.6 StartY=1.45 StartZ=0 EndX=-3 EndY=1.45 EndZ=0
    g4: LineSegment StartX=1.6 StartY=1.45 StartZ=0 EndX=1.6 EndY=-1.45 EndZ=0
    g5: LineSegment StartX=1.6 StartY=-1.45 StartZ=0 EndX=3 EndY=-1.45 EndZ=0
    g6: LineSegment StartX=3 StartY=-1.45 StartZ=0 EndX=3 EndY=1.45 EndZ=0
    g7: LineSegment StartX=3 StartY=1.45 StartZ=0 EndX=1.6 EndY=1.45 EndZ=0
  constraints (24):
    c: Coincident(g0,g1)
    c: Coincident(g1,g2)
    c: Coincident(g2,g3)
    c: Coincident(g3,g0)
    c: Vertical(g0)
    c: Vertical(g2)
    c: Horizontal(g1)
    c: Horizontal(g3)
    c: PointOnObject(g0,g-3)
    c: PointOnObject(g1,g-4)
    c: Coincident(g4,g5)
    c: Coincident(g5,g6)
    c: Coincident(g6,g7)
    c: Coincident(g7,g4)
    c: Vertical(g4)
    c: Vertical(g6)
    c: Horizontal(g5)
    c: Horizontal(g7)
    c: PointOnObject(g4,g-5)
    c: PointOnObject(g5,g-6)
    c: DistanceY(g4,g4) = 2.9
    c: DistanceY(g0,g0) = 2.9
    c: DistanceY(g0,g-3) = 0.9
    c: DistanceY(g4,g-5) = 0.9
FEATURE [PartDesign::Pad] Pad096
  BaseFeature = -> Pad095
  Direction = (0,0,-1)
  Length = 1.6
  Length2 = 10
  Profile = -> Sketch181
  ReferenceAxis = -> Sketch181 [N_Axis]
  Refine = true
  Suppressed = false
  Type = 0
FEATURE [Sketcher::SketchObject] Sketch182
  ArcFitTolerance = 1e-06
  AttachmentSupport = -> [Pad096]
  FullyConstrained = true
  MakeInternals = false
  MapMode = 5
  Placement = pos=(0,0,3e-16) rot=(1,0,0;3.14159rad)
  sketch-geometry (1):
    g0: Circle CenterX=8 CenterY=0 CenterZ=0 NormalX=0 NormalY=0 NormalZ=1 AngleXU=0 Radius=3.5
  constraints (3):
    c: PointOnObject(g0,g-1)
    c: Diameter(g0) = 7
    c: DistanceX(g-1,g0) = 8
FEATURE [PartDesign::Pad] Pad097
  BaseFeature = -> Pad096
  Direction = (0,0,-1)
  Length = 2
  Length2 = 10
  Profile = -> Sketch182
  ReferenceAxis = -> Sketch182 [N_Axis]
  Refine = true
  Suppressed = false
  Type = 0
FEATURE [Sketcher::SketchObject] Sketch183
  ArcFitTolerance = 1e-06
  AttachmentSupport = -> [Pad097]
  ExternalGeometry = -> [Pad097]
  FullyConstrained = true
  MakeInternals = false
  MapMode = 5
  Placement = pos=(0,0,-2) rot=(1,0,0;3.14159rad)
  sketch-geometry (1):
    g0: Circle CenterX=8 CenterY=0 CenterZ=0 NormalX=0 NormalY=0 NormalZ=1 AngleXU=0 Radius=2.45
  constraints (2):
    c: Coincident(g0,g-3)
    c: Diameter(g0) = 4.9
FEATURE [PartDesign::Pocket] Pocket089
  BaseFeature = -> Pad097
  Direction = (0,0,1)
  Length = 2
  Length2 = 5
  Profile = -> Sketch183
  ReferenceAxis = -> Sketch183 [N_Axis]
  Refine = true
  Suppressed = false
  Type = 0
FEATURE [Sketcher::SketchObject] Sketch184
  ArcFitTolerance = 1e-06
  AttachmentSupport = -> [Pocket089]
  ExternalGeometry = -> [Pocket089]
  FullyConstrained = true
  MakeInternals = false
  MapMode = 5
  Placement = pos=(0,0,3e-16) rot=(1,0,0;3.14159rad)
  sketch-geometry (4):
    g0: LineSegment StartX=34.8723 StartY=2 StartZ=0 EndX=34.8723 EndY=-2 EndZ=0
    g1: LineSegment StartX=34.8723 StartY=2 StartZ=0 EndX=10.8723 EndY=2 EndZ=0
    g2: LineSegment StartX=34.8723 StartY=-2 StartZ=0 EndX=10.8723 EndY=-2 EndZ=0
    g3: ArcOfCircle CenterX=8 CenterY=0 CenterZ=0 NormalX=0 NormalY=0 NormalZ=1 AngleXU=0 Radius=3.5 StartAngle=5.67494 EndAngle=6.89143
  constraints (12):
    c: Vertical(g0)
    c: Coincident(g1,g0)
    c: PointOnObject(g1,g-3)
    c: Horizontal(g1)
    c: DistanceY(g-3,g0) = 2
    c: DistanceY(g0,g-3) = 2
    c: Coincident(g2,g0)
    c: Coincident(g3,g2)
    c: Coincident(g3,g1)
    c: Coincident(g3,g-3)
    c: DistanceX(g1,g1) = 24
    c: Horizontal(g2)
FEATURE [PartDesign::Pocket] Pocket090
  BaseFeature = -> Pocket089
  Direction = (0,0,1)
  Length = 1
  Length2 = 5
  Profile = -> Sketch184
  ReferenceAxis = -> Sketch184 [N_Axis]
  Refine = true
  Suppressed = false
  Type = 0
FEATURE [Sketcher::SketchObject] Sketch185
  ArcFitTolerance = 1e-06
  AttachmentSupport = -> [Pocket090]
  ExternalGeometry = -> [Pocket090]
  FullyConstrained = true
  MakeInternals = false
  MapMode = 5
  Placement = pos=(0,0,2e-16) rot=(1,0,0;3.14159rad)
  sketch-geometry (1):
    g0: Circle CenterX=8 CenterY=0 CenterZ=0 NormalX=0 NormalY=0 NormalZ=1 AngleXU=0 Radius=1.25
  constraints (2):
    c: Coincident(g0,g-3)
    c: Diameter(g0) = 2.5
FEATURE [PartDesign::Pocket] Pocket091
  BaseFeature = -> Pocket090
  Direction = (0,0,1)
  Length = 2.6
  Length2 = 5
  Profile = -> Sketch185
  ReferenceAxis = -> Sketch185 [N_Axis]
  Refine = true
  Suppressed = false
  Type = 0
FEATURE [Sketcher::SketchObject] Sketch186
  ArcFitTolerance = 1e-06
  AttachmentSupport = -> [Pocket091]
  ExternalGeometry = -> [Pocket091]
  FullyConstrained = true
  MakeInternals = false
  MapMode = 5
  Placement = pos=(0,0,2.6) rot=(0,0,1;0rad)
  sketch-geometry (1):
    g0: Circle CenterX=8 CenterY=0 CenterZ=0 NormalX=0 NormalY=0 NormalZ=1 AngleXU=0 Radius=1.95
  constraints (2):
    c: Coincident(g0,g-3)
    c: Diameter(g0) = 3.9
FEATURE [PartDesign::Pocket] Pocket092
  BaseFeature = -> Pocket091
  Direction = (0,0,-1)
  Length = 1.8
  Length2 = 5
  Profile = -> Sketch186
  ReferenceAxis = -> Sketch186 [N_Axis]
  Refine = true
  Suppressed = false
  Type = 0
FEATURE [Sketcher::SketchObject] Sketch285
  ArcFitTolerance = 1e-06
  AttachmentSupport = -> [Pocket092]
  ExternalGeometry = -> [Pocket092]
  FullyConstrained = true
  MakeInternals = false
  MapMode = 5
  Placement = pos=(0,0,-6.5) rot=(1,0,0;3.14159rad)
  sketch-geometry (8):
    g0: LineSegment StartX=-3 StartY=1.45 StartZ=0 EndX=-3 EndY=-1.45 EndZ=0
    g1: LineSegment StartX=-3 StartY=-1.45 StartZ=0 EndX=-1.6 EndY=-1.45 EndZ=0
    g2: LineSegment StartX=-1.6 StartY=-1.45 StartZ=0 EndX=-1.6 EndY=1.45 EndZ=0
    g3: LineSegment StartX=-1.6 StartY=1.45 StartZ=0 EndX=-3 EndY=1.45 EndZ=0
    g4: LineSegment StartX=1.6 StartY=1.45 StartZ=0 EndX=1.6 EndY=-1.45 EndZ=0
    g5: LineSegment StartX=1.6 StartY=-1.45 StartZ=0 EndX=3 EndY=-1.45 EndZ=0
    g6: LineSegment StartX=3 StartY=-1.45 StartZ=0 EndX=3 EndY=1.45 EndZ=0
    g7: LineSegment StartX=3 StartY=1.45 StartZ=0 EndX=1.6 EndY=1.45 EndZ=0
  constraints (20):
    c: Coincident(g0,g1)
    c: Coincident(g1,g2)
    c: Coincident(g2,g3)
    c: Coincident(g3,g0)
    c: Vertical(g0)
    c: Vertical(g2)
    c: Horizontal(g1)
    c: Horizontal(g3)
    c: Coincident(g0,g-3)
    c: Coincident(g1,g-4)
    c: Coincident(g4,g5)
    c: Coincident(g5,g6)
    c: Coincident(g6,g7)
    c: Coincident(g7,g4)
    c: Vertical(g4)
    c: Vertical(g6)
    c: Horizontal(g5)
    c: Horizontal(g7)
    c: Coincident(g4,g-5)
    c: Coincident(g5,g-6)
FEATURE [PartDesign::Pad] Pad163
  BaseFeature = -> Pocket092
  Direction = (0,0,-1)
  Length = 0.33
  Length2 = 10
  Profile = -> Sketch285
  ReferenceAxis = -> Sketch285 [N_Axis]
  Refine = true
  Suppressed = false
  Type = 0
FEATURE [PartDesign::Body] Body012  label="Right_Outer_Leg"
  AllowCompound = false
  Group = -> [Sketch130,Pad066,Sketch131,Pad067,Sketch132,Pad068,Sketch133,Pad069,Sketch134,Pocket069,Sketch135,Pocket070,Sketch136,Pad070,Sketch137,Pad071,Fillet032,Sketch138,Pocket071,Sketch139,Pad072,Sketch140,Pocket072,Sketch141,Pocket073,Sketch179,Pad094,Sketch180,Pad095,Sketch181,Pad096,Sketch182,Pad097,Sketch183,Pocket089,Sketch184,Pocket090,Sketch185,Pocket091,Sketch186,Pocket092,Sketch285,Pad163,+3 more]
  Origin = -> Origin014
  Placement = pos=(21.3,-51,-6.5) rot=(-0.58,-0.58,0.58;2.0944rad)
  Tip = -> Pad217
